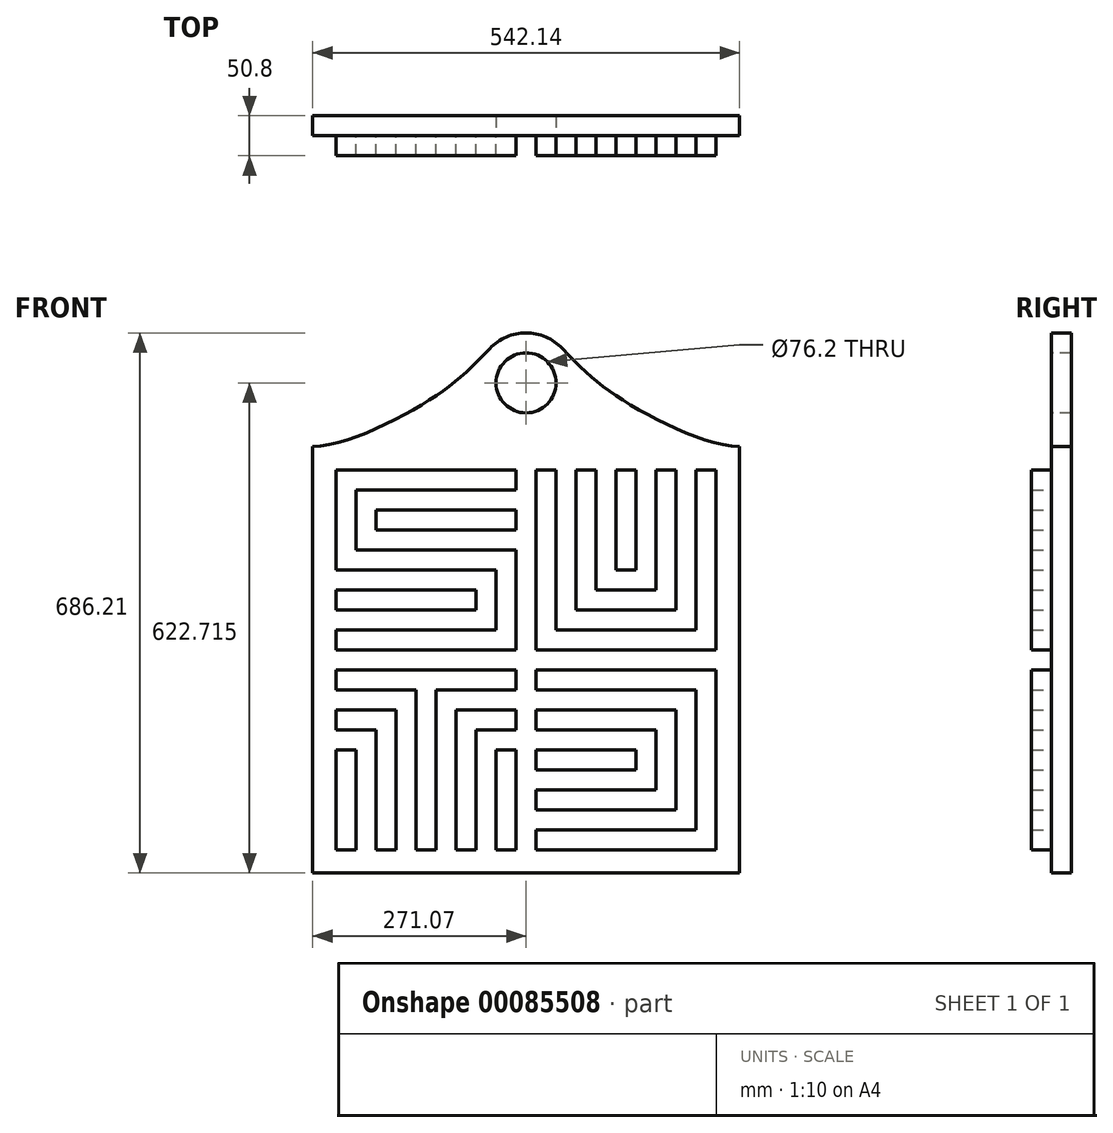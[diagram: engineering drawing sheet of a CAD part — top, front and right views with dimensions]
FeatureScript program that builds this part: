
annotation { "Feature Type Name" : "Feature", "Feature Type Description" : "" }
export const myFeature = defineFeature(function(context is Context, id is Id, definition is map)
    precondition{}
    {
        {
            var Q0;
            Q0=qCreatedBy(makeId("Front.planeOp"),FACE);
            var sketch = newSketch(context, id + "F0", { "sketchPlane" : qUnion([Q0])});
            skLineSegment(sketch, "E0.bottom", {"start": v(-114.3, 114.3) * mm, "end": v(114.3, 114.3) * mm});
            skLineSegment(sketch, "E0.top", {"start": v(-114.3, -114.3) * mm, "end": v(114.3, -114.3) * mm});
            skLineSegment(sketch, "E0.left", {"start": v(-114.3, 114.3) * mm, "end": v(-114.3, -114.3) * mm});
            skLineSegment(sketch, "E0.right", {"start": v(114.3, 114.3) * mm, "end": v(114.3, -114.3) * mm});
            skPoint(sketch, "E0.middle", {"position": v(0, 0) * mm});
            skLineSegment(sketch, "E1.1.0.0", {"start": v(-88.9, 114.3) * mm, "end": v(-88.9, -114.3) * mm});
            skLineSegment(sketch, "E1.2.0.0", {"start": v(-63.5, 114.3) * mm, "end": v(-63.5, -114.3) * mm});
            skLineSegment(sketch, "E1.3.0.0", {"start": v(-38.1, 114.3) * mm, "end": v(-38.1, -114.3) * mm});
            skLineSegment(sketch, "E1.4.0.0", {"start": v(-12.7, 114.3) * mm, "end": v(-12.7, -114.3) * mm});
            skLineSegment(sketch, "E1.5.0.0", {"start": v(12.7, 114.3) * mm, "end": v(12.7, -114.3) * mm});
            skLineSegment(sketch, "E1.6.0.0", {"start": v(38.1, 114.3) * mm, "end": v(38.1, -114.3) * mm});
            skLineSegment(sketch, "E1.7.0.0", {"start": v(63.5, 114.3) * mm, "end": v(63.5, -114.3) * mm});
            skLineSegment(sketch, "E1.8.0.0", {"start": v(88.9, 114.3) * mm, "end": v(88.9, -114.3) * mm});
            skLineSegment(sketch, "E1.direction1", {"start": v(-114.3, -114.3) * mm, "end": v(-88.9, -114.3) * mm, "construction": true});
            skLineSegment(sketch, "E2.0.1.0", {"start": v(-114.3, 88.9) * mm, "end": v(114.3, 88.9) * mm});
            skLineSegment(sketch, "E2.0.2.0", {"start": v(-114.3, 63.5) * mm, "end": v(114.3, 63.5) * mm});
            skLineSegment(sketch, "E2.0.3.0", {"start": v(-114.3, 38.1) * mm, "end": v(114.3, 38.1) * mm});
            skLineSegment(sketch, "E2.0.4.0", {"start": v(-114.3, 12.7) * mm, "end": v(114.3, 12.7) * mm});
            skLineSegment(sketch, "E2.0.5.0", {"start": v(-114.3, -12.7) * mm, "end": v(114.3, -12.7) * mm});
            skLineSegment(sketch, "E2.0.6.0", {"start": v(-114.3, -38.1) * mm, "end": v(114.3, -38.1) * mm});
            skLineSegment(sketch, "E2.0.7.0", {"start": v(-114.3, -63.5) * mm, "end": v(114.3, -63.5) * mm});
            skLineSegment(sketch, "E2.0.8.0", {"start": v(-114.3, -88.9) * mm, "end": v(114.3, -88.9) * mm});
            skLineSegment(sketch, "E2.direction1", {"start": v(-114.3, 114.3) * mm, "end": v(-88.9, 114.3) * mm, "construction": true});
            skLineSegment(sketch, "E2.direction2", {"start": v(-114.3, 114.3) * mm, "end": v(-114.3, 88.9) * mm, "construction": true});
            skLineSegment(sketch, "E3.0.1.0", {"start": v(-12.7, -139.7) * mm, "end": v(-12.7, -368.3) * mm});
            skLineSegment(sketch, "E3.0.1.1", {"start": v(-88.9, -139.7) * mm, "end": v(-88.9, -368.3) * mm});
            skLineSegment(sketch, "E3.0.1.2", {"start": v(-38.1, -139.7) * mm, "end": v(-38.1, -368.3) * mm});
            skLineSegment(sketch, "E3.0.1.3", {"start": v(-114.3, -165.1) * mm, "end": v(114.3, -165.1) * mm});
            skLineSegment(sketch, "E3.0.1.4", {"start": v(-114.3, -190.5) * mm, "end": v(114.3, -190.5) * mm});
            skLineSegment(sketch, "E3.0.1.5", {"start": v(-63.5, -139.7) * mm, "end": v(-63.5, -368.3) * mm});
            skLineSegment(sketch, "E3.0.1.6", {"start": v(-114.3, -215.9) * mm, "end": v(114.3, -215.9) * mm});
            skLineSegment(sketch, "E3.0.1.7", {"start": v(-114.3, -139.7) * mm, "end": v(114.3, -139.7) * mm});
            skLineSegment(sketch, "E3.0.1.8", {"start": v(-114.3, -368.3) * mm, "end": v(114.3, -368.3) * mm});
            skLineSegment(sketch, "E3.0.1.9", {"start": v(-114.3, -139.7) * mm, "end": v(-114.3, -368.3) * mm});
            skLineSegment(sketch, "E3.0.1.10", {"start": v(114.3, -139.7) * mm, "end": v(114.3, -368.3) * mm});
            skLineSegment(sketch, "E3.0.1.11", {"start": v(12.7, -139.7) * mm, "end": v(12.7, -368.3) * mm});
            skLineSegment(sketch, "E3.0.1.12", {"start": v(38.1, -139.7) * mm, "end": v(38.1, -368.3) * mm});
            skLineSegment(sketch, "E3.0.1.13", {"start": v(63.5, -139.7) * mm, "end": v(63.5, -368.3) * mm});
            skLineSegment(sketch, "E3.0.1.14", {"start": v(88.9, -139.7) * mm, "end": v(88.9, -368.3) * mm});
            skLineSegment(sketch, "E3.0.1.15", {"start": v(-114.3, -241.3) * mm, "end": v(114.3, -241.3) * mm});
            skLineSegment(sketch, "E3.0.1.16", {"start": v(-114.3, -266.7) * mm, "end": v(114.3, -266.7) * mm});
            skPoint(sketch, "E3.0.1.17", {"position": v(0, -254) * mm});
            skLineSegment(sketch, "E3.0.1.18", {"start": v(-114.3, -342.9) * mm, "end": v(114.3, -342.9) * mm});
            skLineSegment(sketch, "E3.0.1.19", {"start": v(-114.3, -292.1) * mm, "end": v(114.3, -292.1) * mm});
            skLineSegment(sketch, "E3.0.1.20", {"start": v(-114.3, -317.5) * mm, "end": v(114.3, -317.5) * mm});
            skLineSegment(sketch, "E3.0.1.21", {"start": v(-114.3, -139.7) * mm, "end": v(-114.3, -165.1) * mm, "construction": true});
            skLineSegment(sketch, "E3.0.1.22", {"start": v(-114.3, -368.3) * mm, "end": v(-88.9, -368.3) * mm, "construction": true});
            skLineSegment(sketch, "E3.0.1.23", {"start": v(-114.3, -139.7) * mm, "end": v(-88.9, -139.7) * mm, "construction": true});
            skLineSegment(sketch, "E3.1.0.0", {"start": v(241.3, 114.3) * mm, "end": v(241.3, -88.9) * mm});
            skLineSegment(sketch, "E3.1.0.1", {"start": v(165.1, 114.3) * mm, "end": v(165.1, -88.9) * mm});
            skLineSegment(sketch, "E3.1.0.2", {"start": v(215.9, 114.3) * mm, "end": v(215.9, -88.9) * mm});
            skLineSegment(sketch, "E3.1.0.3", {"start": v(165.1, 88.9) * mm, "end": v(190.5, 88.9) * mm});
            skLineSegment(sketch, "E3.1.0.4", {"start": v(165.1, 63.5) * mm, "end": v(342.9, 63.5) * mm});
            skLineSegment(sketch, "E3.1.0.5", {"start": v(190.5, 114.3) * mm, "end": v(190.5, -88.9) * mm});
            skLineSegment(sketch, "E3.1.0.6", {"start": v(165.1, 38.1) * mm, "end": v(342.9, 38.1) * mm});
            skLineSegment(sketch, "E3.1.0.7", {"start": v(139.7, 114.3) * mm, "end": v(368.3, 114.3) * mm});
            skLineSegment(sketch, "E3.1.0.8", {"start": v(139.7, -114.3) * mm, "end": v(368.3, -114.3) * mm});
            skLineSegment(sketch, "E3.1.0.9", {"start": v(139.7, 114.3) * mm, "end": v(139.7, -114.3) * mm});
            skLineSegment(sketch, "E3.1.0.10", {"start": v(368.3, 114.3) * mm, "end": v(368.3, -114.3) * mm});
            skLineSegment(sketch, "E3.1.0.11", {"start": v(266.7, 114.3) * mm, "end": v(266.7, -88.9) * mm});
            skLineSegment(sketch, "E3.1.0.12", {"start": v(292.1, 114.3) * mm, "end": v(292.1, -88.9) * mm});
            skLineSegment(sketch, "E3.1.0.13", {"start": v(317.5, 114.3) * mm, "end": v(317.5, -88.9) * mm});
            skLineSegment(sketch, "E3.1.0.14", {"start": v(342.9, 114.3) * mm, "end": v(342.9, -88.9) * mm});
            skLineSegment(sketch, "E3.1.0.15", {"start": v(165.1, 12.7) * mm, "end": v(342.9, 12.7) * mm});
            skLineSegment(sketch, "E3.1.0.16", {"start": v(165.1, -12.7) * mm, "end": v(342.9, -12.7) * mm});
            skPoint(sketch, "E3.1.0.17", {"position": v(254, 0) * mm});
            skLineSegment(sketch, "E3.1.0.18", {"start": v(165.1, -88.9) * mm, "end": v(342.9, -88.9) * mm});
            skLineSegment(sketch, "E3.1.0.19", {"start": v(165.1, -38.1) * mm, "end": v(342.9, -38.1) * mm});
            skLineSegment(sketch, "E3.1.0.20", {"start": v(165.1, -63.5) * mm, "end": v(342.9, -63.5) * mm});
            skLineSegment(sketch, "E3.1.0.21", {"start": v(139.7, 114.3) * mm, "end": v(139.7, 88.9) * mm, "construction": true});
            skLineSegment(sketch, "E3.1.0.22", {"start": v(139.7, -114.3) * mm, "end": v(165.1, -114.3) * mm, "construction": true});
            skLineSegment(sketch, "E3.1.0.23", {"start": v(139.7, 114.3) * mm, "end": v(165.1, 114.3) * mm, "construction": true});
            skLineSegment(sketch, "E3.1.1.0", {"start": v(241.3, -139.7) * mm, "end": v(241.3, -368.3) * mm});
            skLineSegment(sketch, "E3.1.1.1", {"start": v(165.1, -139.7) * mm, "end": v(165.1, -368.3) * mm});
            skLineSegment(sketch, "E3.1.1.2", {"start": v(215.9, -139.7) * mm, "end": v(215.9, -368.3) * mm});
            skLineSegment(sketch, "E3.1.1.3", {"start": v(139.7, -165.1) * mm, "end": v(368.3, -165.1) * mm});
            skLineSegment(sketch, "E3.1.1.4", {"start": v(139.7, -190.5) * mm, "end": v(368.3, -190.5) * mm});
            skLineSegment(sketch, "E3.1.1.5", {"start": v(190.5, -139.7) * mm, "end": v(190.5, -368.3) * mm});
            skLineSegment(sketch, "E3.1.1.6", {"start": v(139.7, -215.9) * mm, "end": v(368.3, -215.9) * mm});
            skLineSegment(sketch, "E3.1.1.7", {"start": v(139.7, -139.7) * mm, "end": v(368.3, -139.7) * mm});
            skLineSegment(sketch, "E3.1.1.8", {"start": v(139.7, -368.3) * mm, "end": v(368.3, -368.3) * mm});
            skLineSegment(sketch, "E3.1.1.9", {"start": v(139.7, -139.7) * mm, "end": v(139.7, -368.3) * mm});
            skLineSegment(sketch, "E3.1.1.10", {"start": v(368.3, -139.7) * mm, "end": v(368.3, -368.3) * mm});
            skLineSegment(sketch, "E3.1.1.11", {"start": v(266.7, -139.7) * mm, "end": v(266.7, -368.3) * mm});
            skLineSegment(sketch, "E3.1.1.12", {"start": v(292.1, -139.7) * mm, "end": v(292.1, -368.3) * mm});
            skLineSegment(sketch, "E3.1.1.13", {"start": v(317.5, -139.7) * mm, "end": v(317.5, -368.3) * mm});
            skLineSegment(sketch, "E3.1.1.14", {"start": v(342.9, -139.7) * mm, "end": v(342.9, -368.3) * mm});
            skLineSegment(sketch, "E3.1.1.15", {"start": v(139.7, -241.3) * mm, "end": v(368.3, -241.3) * mm});
            skLineSegment(sketch, "E3.1.1.16", {"start": v(139.7, -266.7) * mm, "end": v(368.3, -266.7) * mm});
            skPoint(sketch, "E3.1.1.17", {"position": v(254, -254) * mm});
            skLineSegment(sketch, "E3.1.1.18", {"start": v(139.7, -342.9) * mm, "end": v(368.3, -342.9) * mm});
            skLineSegment(sketch, "E3.1.1.19", {"start": v(139.7, -292.1) * mm, "end": v(368.3, -292.1) * mm});
            skLineSegment(sketch, "E3.1.1.20", {"start": v(139.7, -317.5) * mm, "end": v(368.3, -317.5) * mm});
            skLineSegment(sketch, "E3.1.1.21", {"start": v(139.7, -139.7) * mm, "end": v(139.7, -165.1) * mm, "construction": true});
            skLineSegment(sketch, "E3.1.1.22", {"start": v(139.7, -368.3) * mm, "end": v(165.1, -368.3) * mm, "construction": true});
            skLineSegment(sketch, "E3.1.1.23", {"start": v(139.7, -139.7) * mm, "end": v(165.1, -139.7) * mm, "construction": true});
            skLineSegment(sketch, "E3.direction1", {"start": v(-12.7, -114.3) * mm, "end": v(241.3, -114.3) * mm, "construction": true});
            skLineSegment(sketch, "E3.direction2", {"start": v(-12.7, -114.3) * mm, "end": v(-12.7, -368.3) * mm, "construction": true});
            skPoint(sketch, "E4.orphan", {"position": v(139.7, 63.5) * mm});
            skPoint(sketch, "E5.orphan", {"position": v(139.7, 38.1) * mm});
            skPoint(sketch, "E6.orphan", {"position": v(139.7, 12.7) * mm});
            skPoint(sketch, "E7.orphan", {"position": v(139.7, -12.7) * mm});
            skPoint(sketch, "E8.orphan", {"position": v(139.7, -38.1) * mm});
            skPoint(sketch, "E9.orphan", {"position": v(139.7, -63.5) * mm});
            skPoint(sketch, "E10.orphan", {"position": v(139.7, -88.9) * mm});
            skPoint(sketch, "E11.orphan", {"position": v(190.5, -114.3) * mm});
            skPoint(sketch, "E12.orphan", {"position": v(215.9, -114.3) * mm});
            skPoint(sketch, "E13.orphan", {"position": v(266.7, -114.3) * mm});
            skPoint(sketch, "E14.orphan", {"position": v(292.1, -114.3) * mm});
            skPoint(sketch, "E15.orphan", {"position": v(317.5, -114.3) * mm});
            skPoint(sketch, "E16.orphan", {"position": v(342.9, -114.3) * mm});
            skPoint(sketch, "E17.orphan", {"position": v(368.3, -88.9) * mm});
            skPoint(sketch, "E18.orphan", {"position": v(368.3, -63.5) * mm});
            skPoint(sketch, "E19.orphan", {"position": v(368.3, -38.1) * mm});
            skPoint(sketch, "E20.orphan", {"position": v(368.3, -12.7) * mm});
            skPoint(sketch, "E21.orphan", {"position": v(368.3, 12.7) * mm});
            skPoint(sketch, "E22.orphan", {"position": v(368.3, 38.1) * mm});
            skPoint(sketch, "E23.orphan", {"position": v(368.3, 63.5) * mm});
            skPoint(sketch, "E24.orphan", {"position": v(368.3, 88.9) * mm});
            skLineSegment(sketch, "E25.trimOffspring", {"start": v(215.9, 88.9) * mm, "end": v(342.9, 88.9) * mm});
            skSolve(sketch);
        }
        {
            var Q0;
            {var subQ0=sQuery(id+"F0.wireOp",EDGE,"E0.right");var subQ1=sQuery(id+"F0.wireOp",EDGE,"E0.bottom");var subQ2=makeQuery(id+"F0.imprint","INTERSECT",VERTEX,{"derivedFrom":[subQ1,subQ0]});Q0=makeQuery(id+"F0.imprint","IMPRINT",FACE,{"disambiguationData":[TD([[makeQuery(id+"F0.imprint","IMPRINT",EDGE,{"disambiguationData":[TD([[subQ2,1.0]])],"derivedFrom":subQ1}),-1.0]])]});}
            var Q1;
            {var subQ0=sQuery(id+"F0.wireOp",EDGE,"E1.7.0.0");var subQ1=sQuery(id+"F0.wireOp",EDGE,"E0.bottom");var subQ2=makeQuery(id+"F0.imprint","INTERSECT",VERTEX,{"derivedFrom":[subQ1,subQ0]});Q1=makeQuery(id+"F0.imprint","IMPRINT",FACE,{"disambiguationData":[TD([[makeQuery(id+"F0.imprint","IMPRINT",EDGE,{"disambiguationData":[TD([[subQ2,-1.0]])],"derivedFrom":subQ1}),-1.0]])]});}
            var Q2;
            {var subQ0=sQuery(id+"F0.wireOp",EDGE,"E1.6.0.0");var subQ1=sQuery(id+"F0.wireOp",EDGE,"E0.bottom");var subQ2=makeQuery(id+"F0.imprint","INTERSECT",VERTEX,{"derivedFrom":[subQ1,subQ0]});Q2=makeQuery(id+"F0.imprint","IMPRINT",FACE,{"disambiguationData":[TD([[makeQuery(id+"F0.imprint","IMPRINT",EDGE,{"disambiguationData":[TD([[subQ2,-1.0]])],"derivedFrom":subQ1}),-1.0]])]});}
            var Q3;
            {var subQ0=sQuery(id+"F0.wireOp",EDGE,"E1.5.0.0");var subQ1=sQuery(id+"F0.wireOp",EDGE,"E0.bottom");var subQ2=makeQuery(id+"F0.imprint","INTERSECT",VERTEX,{"derivedFrom":[subQ1,subQ0]});Q3=makeQuery(id+"F0.imprint","IMPRINT",FACE,{"disambiguationData":[TD([[makeQuery(id+"F0.imprint","IMPRINT",EDGE,{"disambiguationData":[TD([[subQ2,-1.0]])],"derivedFrom":subQ1}),-1.0]])]});}
            var Q4;
            {var subQ0=sQuery(id+"F0.wireOp",EDGE,"E1.4.0.0");var subQ1=sQuery(id+"F0.wireOp",EDGE,"E0.bottom");var subQ2=makeQuery(id+"F0.imprint","INTERSECT",VERTEX,{"derivedFrom":[subQ1,subQ0]});Q4=makeQuery(id+"F0.imprint","IMPRINT",FACE,{"disambiguationData":[TD([[makeQuery(id+"F0.imprint","IMPRINT",EDGE,{"disambiguationData":[TD([[subQ2,-1.0]])],"derivedFrom":subQ1}),-1.0]])]});}
            var Q5;
            {var subQ0=sQuery(id+"F0.wireOp",EDGE,"E1.3.0.0");var subQ1=sQuery(id+"F0.wireOp",EDGE,"E0.bottom");var subQ2=makeQuery(id+"F0.imprint","INTERSECT",VERTEX,{"derivedFrom":[subQ1,subQ0]});Q5=makeQuery(id+"F0.imprint","IMPRINT",FACE,{"disambiguationData":[TD([[makeQuery(id+"F0.imprint","IMPRINT",EDGE,{"disambiguationData":[TD([[subQ2,-1.0]])],"derivedFrom":subQ1}),-1.0]])]});}
            var Q6;
            {var subQ0=sQuery(id+"F0.wireOp",EDGE,"E1.2.0.0");var subQ1=sQuery(id+"F0.wireOp",EDGE,"E0.bottom");var subQ2=makeQuery(id+"F0.imprint","INTERSECT",VERTEX,{"derivedFrom":[subQ1,subQ0]});Q6=makeQuery(id+"F0.imprint","IMPRINT",FACE,{"disambiguationData":[TD([[makeQuery(id+"F0.imprint","IMPRINT",EDGE,{"disambiguationData":[TD([[subQ2,-1.0]])],"derivedFrom":subQ1}),-1.0]])]});}
            var Q7;
            {var subQ0=sQuery(id+"F0.wireOp",EDGE,"E1.1.0.0");var subQ1=sQuery(id+"F0.wireOp",EDGE,"E0.bottom");var subQ2=makeQuery(id+"F0.imprint","INTERSECT",VERTEX,{"derivedFrom":[subQ1,subQ0]});Q7=makeQuery(id+"F0.imprint","IMPRINT",FACE,{"disambiguationData":[TD([[makeQuery(id+"F0.imprint","IMPRINT",EDGE,{"disambiguationData":[TD([[subQ2,-1.0]])],"derivedFrom":subQ1}),-1.0]])]});}
            var Q8;
            {var subQ0=sQuery(id+"F0.wireOp",EDGE,"E0.left");var subQ1=sQuery(id+"F0.wireOp",EDGE,"E0.bottom");var subQ2=makeQuery(id+"F0.imprint","INTERSECT",VERTEX,{"derivedFrom":[subQ1,subQ0]});Q8=makeQuery(id+"F0.imprint","IMPRINT",FACE,{"disambiguationData":[TD([[makeQuery(id+"F0.imprint","IMPRINT",EDGE,{"disambiguationData":[TD([[subQ2,-1.0]])],"derivedFrom":subQ1}),-1.0]])]});}
            var Q9;
            {var subQ0=sQuery(id+"F0.wireOp",EDGE,"E2.0.1.0");var subQ1=sQuery(id+"F0.wireOp",EDGE,"E0.left");var subQ2=makeQuery(id+"F0.imprint","INTERSECT",VERTEX,{"derivedFrom":[subQ1,subQ0]});Q9=makeQuery(id+"F0.imprint","IMPRINT",FACE,{"disambiguationData":[TD([[makeQuery(id+"F0.imprint","IMPRINT",EDGE,{"disambiguationData":[TD([[subQ2,-1.0]])],"derivedFrom":subQ1}),1.0]])]});}
            var Q10;
            {var subQ0=sQuery(id+"F0.wireOp",EDGE,"E2.0.2.0");var subQ1=sQuery(id+"F0.wireOp",EDGE,"E0.left");var subQ2=makeQuery(id+"F0.imprint","INTERSECT",VERTEX,{"derivedFrom":[subQ1,subQ0]});Q10=makeQuery(id+"F0.imprint","IMPRINT",FACE,{"disambiguationData":[TD([[makeQuery(id+"F0.imprint","IMPRINT",EDGE,{"disambiguationData":[TD([[subQ2,-1.0]])],"derivedFrom":subQ1}),1.0]])]});}
            var Q11;
            {var subQ0=sQuery(id+"F0.wireOp",EDGE,"E2.0.3.0");var subQ1=sQuery(id+"F0.wireOp",EDGE,"E0.left");var subQ2=makeQuery(id+"F0.imprint","INTERSECT",VERTEX,{"derivedFrom":[subQ1,subQ0]});Q11=makeQuery(id+"F0.imprint","IMPRINT",FACE,{"disambiguationData":[TD([[makeQuery(id+"F0.imprint","IMPRINT",EDGE,{"disambiguationData":[TD([[subQ2,-1.0]])],"derivedFrom":subQ1}),1.0]])]});}
            var Q12;
            {var subQ0=sQuery(id+"F0.wireOp",EDGE,"E2.0.4.0");var subQ1=sQuery(id+"F0.wireOp",EDGE,"E0.left");var subQ2=makeQuery(id+"F0.imprint","INTERSECT",VERTEX,{"derivedFrom":[subQ1,subQ0]});Q12=makeQuery(id+"F0.imprint","IMPRINT",FACE,{"disambiguationData":[TD([[makeQuery(id+"F0.imprint","IMPRINT",EDGE,{"disambiguationData":[TD([[subQ2,-1.0]])],"derivedFrom":subQ1}),1.0]])]});}
            var Q13;
            {var subQ0=sQuery(id+"F0.wireOp",EDGE,"E2.0.4.0");var subQ1=sQuery(id+"F0.wireOp",EDGE,"E1.1.0.0");var subQ2=makeQuery(id+"F0.imprint","INTERSECT",VERTEX,{"derivedFrom":[subQ1,subQ0]});Q13=makeQuery(id+"F0.imprint","IMPRINT",FACE,{"disambiguationData":[TD([[makeQuery(id+"F0.imprint","IMPRINT",EDGE,{"disambiguationData":[TD([[subQ2,-1.0]])],"derivedFrom":subQ1}),1.0]])]});}
            var Q14;
            {var subQ0=sQuery(id+"F0.wireOp",EDGE,"E2.0.4.0");var subQ1=sQuery(id+"F0.wireOp",EDGE,"E1.2.0.0");var subQ2=makeQuery(id+"F0.imprint","INTERSECT",VERTEX,{"derivedFrom":[subQ1,subQ0]});Q14=makeQuery(id+"F0.imprint","IMPRINT",FACE,{"disambiguationData":[TD([[makeQuery(id+"F0.imprint","IMPRINT",EDGE,{"disambiguationData":[TD([[subQ2,-1.0]])],"derivedFrom":subQ1}),1.0]])]});}
            var Q15;
            {var subQ0=sQuery(id+"F0.wireOp",EDGE,"E2.0.4.0");var subQ1=sQuery(id+"F0.wireOp",EDGE,"E1.3.0.0");var subQ2=makeQuery(id+"F0.imprint","INTERSECT",VERTEX,{"derivedFrom":[subQ1,subQ0]});Q15=makeQuery(id+"F0.imprint","IMPRINT",FACE,{"disambiguationData":[TD([[makeQuery(id+"F0.imprint","IMPRINT",EDGE,{"disambiguationData":[TD([[subQ2,-1.0]])],"derivedFrom":subQ1}),1.0]])]});}
            var Q16;
            {var subQ0=sQuery(id+"F0.wireOp",EDGE,"E2.0.4.0");var subQ1=sQuery(id+"F0.wireOp",EDGE,"E1.4.0.0");var subQ2=makeQuery(id+"F0.imprint","INTERSECT",VERTEX,{"derivedFrom":[subQ1,subQ0]});Q16=makeQuery(id+"F0.imprint","IMPRINT",FACE,{"disambiguationData":[TD([[makeQuery(id+"F0.imprint","IMPRINT",EDGE,{"disambiguationData":[TD([[subQ2,-1.0]])],"derivedFrom":subQ1}),1.0]])]});}
            var Q17;
            {var subQ0=sQuery(id+"F0.wireOp",EDGE,"E2.0.4.0");var subQ1=sQuery(id+"F0.wireOp",EDGE,"E1.5.0.0");var subQ2=makeQuery(id+"F0.imprint","INTERSECT",VERTEX,{"derivedFrom":[subQ1,subQ0]});Q17=makeQuery(id+"F0.imprint","IMPRINT",FACE,{"disambiguationData":[TD([[makeQuery(id+"F0.imprint","IMPRINT",EDGE,{"disambiguationData":[TD([[subQ2,-1.0]])],"derivedFrom":subQ1}),1.0]])]});}
            var Q18;
            {var subQ0=sQuery(id+"F0.wireOp",EDGE,"E2.0.4.0");var subQ1=sQuery(id+"F0.wireOp",EDGE,"E1.6.0.0");var subQ2=makeQuery(id+"F0.imprint","INTERSECT",VERTEX,{"derivedFrom":[subQ1,subQ0]});Q18=makeQuery(id+"F0.imprint","IMPRINT",FACE,{"disambiguationData":[TD([[makeQuery(id+"F0.imprint","IMPRINT",EDGE,{"disambiguationData":[TD([[subQ2,-1.0]])],"derivedFrom":subQ1}),1.0]])]});}
            var Q19;
            {var subQ0=sQuery(id+"F0.wireOp",EDGE,"E2.0.4.0");var subQ1=sQuery(id+"F0.wireOp",EDGE,"E1.7.0.0");var subQ2=makeQuery(id+"F0.imprint","INTERSECT",VERTEX,{"derivedFrom":[subQ1,subQ0]});Q19=makeQuery(id+"F0.imprint","IMPRINT",FACE,{"disambiguationData":[TD([[makeQuery(id+"F0.imprint","IMPRINT",EDGE,{"disambiguationData":[TD([[subQ2,-1.0]])],"derivedFrom":subQ1}),1.0]])]});}
            var Q20;
            {var subQ0=sQuery(id+"F0.wireOp",EDGE,"E2.0.4.0");var subQ1=sQuery(id+"F0.wireOp",EDGE,"E0.right");var subQ2=makeQuery(id+"F0.imprint","INTERSECT",VERTEX,{"derivedFrom":[subQ1,subQ0]});Q20=makeQuery(id+"F0.imprint","IMPRINT",FACE,{"disambiguationData":[TD([[makeQuery(id+"F0.imprint","IMPRINT",EDGE,{"disambiguationData":[TD([[subQ2,-1.0]])],"derivedFrom":subQ1}),-1.0]])]});}
            extrude(context, id + "F1", {"entities" : qUnion([Q0, Q1, Q2, Q3, Q4, Q5, Q6, Q7, Q8, Q9, Q10, Q11, Q12, Q13, Q14, Q15, Q16, Q17, Q18, Q19, Q20]), "depth" : 25.4 * mm});
        }
        {
            var Q0;
            Q0=makeQuery(id+"F0.imprint","IMPRINT",FACE,{"disambiguationData":[TD([[makeQuery(id+"F0.imprint","IMPRINT",EDGE,{"derivedFrom":sQuery(id+"F0.wireOp",EDGE,"E3.1.0.8")}),1.0]])]});
            var Q1;
            {var subQ1=sQuery(id+"F0.wireOp",EDGE,"E3.1.0.2");var subQ6=sQuery(id+"F0.wireOp",EDGE,"E3.1.0.7");var subQ9=makeQuery(id+"F0.imprint","INTERSECT",VERTEX,{"derivedFrom":[subQ1,subQ6]});Q1=makeQuery(id+"F0.imprint","IMPRINT",FACE,{"disambiguationData":[TD([[makeQuery(id+"F0.imprint","IMPRINT",EDGE,{"disambiguationData":[TD([[subQ9,-1.0]])],"derivedFrom":subQ1}),-1.0]])]});}
            var Q2;
            {var subQ0=sQuery(id+"F0.wireOp",EDGE,"E3.1.0.4");var subQ1=sQuery(id+"F0.wireOp",EDGE,"E3.1.0.2");var subQ2=makeQuery(id+"F0.imprint","INTERSECT",VERTEX,{"derivedFrom":[subQ1,subQ0]});Q2=makeQuery(id+"F0.imprint","IMPRINT",FACE,{"disambiguationData":[TD([[makeQuery(id+"F0.imprint","IMPRINT",EDGE,{"disambiguationData":[TD([[subQ2,-1.0]])],"derivedFrom":subQ1}),-1.0]])]});}
            var Q3;
            {var subQ0=sQuery(id+"F0.wireOp",EDGE,"E3.1.0.6");var subQ1=sQuery(id+"F0.wireOp",EDGE,"E3.1.0.2");var subQ2=makeQuery(id+"F0.imprint","INTERSECT",VERTEX,{"derivedFrom":[subQ1,subQ0]});Q3=makeQuery(id+"F0.imprint","IMPRINT",FACE,{"disambiguationData":[TD([[makeQuery(id+"F0.imprint","IMPRINT",EDGE,{"disambiguationData":[TD([[subQ2,-1.0]])],"derivedFrom":subQ1}),-1.0]])]});}
            var Q4;
            {var subQ0=sQuery(id+"F0.wireOp",EDGE,"E3.1.0.15");var subQ1=sQuery(id+"F0.wireOp",EDGE,"E3.1.0.2");var subQ2=makeQuery(id+"F0.imprint","INTERSECT",VERTEX,{"derivedFrom":[subQ1,subQ0]});Q4=makeQuery(id+"F0.imprint","IMPRINT",FACE,{"disambiguationData":[TD([[makeQuery(id+"F0.imprint","IMPRINT",EDGE,{"disambiguationData":[TD([[subQ2,-1.0]])],"derivedFrom":subQ1}),-1.0]])]});}
            var Q5;
            {var subQ0=sQuery(id+"F0.wireOp",EDGE,"E3.1.0.16");var subQ1=sQuery(id+"F0.wireOp",EDGE,"E3.1.0.2");var subQ2=makeQuery(id+"F0.imprint","INTERSECT",VERTEX,{"derivedFrom":[subQ1,subQ0]});Q5=makeQuery(id+"F0.imprint","IMPRINT",FACE,{"disambiguationData":[TD([[makeQuery(id+"F0.imprint","IMPRINT",EDGE,{"disambiguationData":[TD([[subQ2,-1.0]])],"derivedFrom":subQ1}),-1.0]])]});}
            var Q6;
            {var subQ0=sQuery(id+"F0.wireOp",EDGE,"E3.1.0.19");var subQ1=sQuery(id+"F0.wireOp",EDGE,"E3.1.0.2");var subQ2=makeQuery(id+"F0.imprint","INTERSECT",VERTEX,{"derivedFrom":[subQ1,subQ0]});Q6=makeQuery(id+"F0.imprint","IMPRINT",FACE,{"disambiguationData":[TD([[makeQuery(id+"F0.imprint","IMPRINT",EDGE,{"disambiguationData":[TD([[subQ2,-1.0]])],"derivedFrom":subQ1}),-1.0]])]});}
            var Q7;
            {var subQ0=sQuery(id+"F0.wireOp",EDGE,"E3.1.0.19");var subQ1=sQuery(id+"F0.wireOp",EDGE,"E3.1.0.11");var subQ2=makeQuery(id+"F0.imprint","INTERSECT",VERTEX,{"derivedFrom":[subQ1,subQ0]});Q7=makeQuery(id+"F0.imprint","IMPRINT",FACE,{"disambiguationData":[TD([[makeQuery(id+"F0.imprint","IMPRINT",EDGE,{"disambiguationData":[TD([[subQ2,-1.0]])],"derivedFrom":subQ1}),1.0]])]});}
            var Q8;
            {var subQ0=sQuery(id+"F0.wireOp",EDGE,"E3.1.0.19");var subQ1=sQuery(id+"F0.wireOp",EDGE,"E3.1.0.12");var subQ2=makeQuery(id+"F0.imprint","INTERSECT",VERTEX,{"derivedFrom":[subQ1,subQ0]});Q8=makeQuery(id+"F0.imprint","IMPRINT",FACE,{"disambiguationData":[TD([[makeQuery(id+"F0.imprint","IMPRINT",EDGE,{"disambiguationData":[TD([[subQ2,-1.0]])],"derivedFrom":subQ1}),1.0]])]});}
            var Q9;
            {var subQ0=sQuery(id+"F0.wireOp",EDGE,"E3.1.0.19");var subQ1=sQuery(id+"F0.wireOp",EDGE,"E3.1.0.0");var subQ2=makeQuery(id+"F0.imprint","INTERSECT",VERTEX,{"derivedFrom":[subQ1,subQ0]});Q9=makeQuery(id+"F0.imprint","IMPRINT",FACE,{"disambiguationData":[TD([[makeQuery(id+"F0.imprint","IMPRINT",EDGE,{"disambiguationData":[TD([[subQ2,-1.0]])],"derivedFrom":subQ1}),-1.0]])]});}
            var Q10;
            {var subQ0=sQuery(id+"F0.wireOp",EDGE,"E3.1.0.19");var subQ1=sQuery(id+"F0.wireOp",EDGE,"E3.1.0.0");var subQ2=makeQuery(id+"F0.imprint","INTERSECT",VERTEX,{"derivedFrom":[subQ1,subQ0]});Q10=makeQuery(id+"F0.imprint","IMPRINT",FACE,{"disambiguationData":[TD([[makeQuery(id+"F0.imprint","IMPRINT",EDGE,{"disambiguationData":[TD([[subQ2,-1.0]])],"derivedFrom":subQ1}),1.0]])]});}
            var Q11;
            {var subQ0=sQuery(id+"F0.wireOp",EDGE,"E3.1.0.12");var subQ1=sQuery(id+"F0.wireOp",EDGE,"E3.1.0.4");var subQ2=makeQuery(id+"F0.imprint","INTERSECT",VERTEX,{"derivedFrom":[subQ1,subQ0]});Q11=makeQuery(id+"F0.imprint","IMPRINT",FACE,{"disambiguationData":[TD([[makeQuery(id+"F0.imprint","IMPRINT",EDGE,{"disambiguationData":[TD([[subQ2,-1.0]])],"derivedFrom":subQ1}),1.0]])]});}
            var Q12;
            {var subQ0=sQuery(id+"F0.wireOp",EDGE,"E3.1.0.12");var subQ1=sQuery(id+"F0.wireOp",EDGE,"E3.1.0.7");var subQ2=makeQuery(id+"F0.imprint","INTERSECT",VERTEX,{"derivedFrom":[subQ1,subQ0]});Q12=makeQuery(id+"F0.imprint","IMPRINT",FACE,{"disambiguationData":[TD([[makeQuery(id+"F0.imprint","IMPRINT",EDGE,{"disambiguationData":[TD([[subQ2,-1.0]])],"derivedFrom":subQ1}),-1.0]])]});}
            var Q13;
            {var subQ0=sQuery(id+"F0.wireOp",EDGE,"E3.1.0.12");var subQ1=sQuery(id+"F0.wireOp",EDGE,"E3.1.0.6");var subQ2=makeQuery(id+"F0.imprint","INTERSECT",VERTEX,{"derivedFrom":[subQ1,subQ0]});Q13=makeQuery(id+"F0.imprint","IMPRINT",FACE,{"disambiguationData":[TD([[makeQuery(id+"F0.imprint","IMPRINT",EDGE,{"disambiguationData":[TD([[subQ2,-1.0]])],"derivedFrom":subQ1}),-1.0]])]});}
            var Q14;
            {var subQ0=sQuery(id+"F0.wireOp",EDGE,"E3.1.0.15");var subQ1=sQuery(id+"F0.wireOp",EDGE,"E3.1.0.12");var subQ2=makeQuery(id+"F0.imprint","INTERSECT",VERTEX,{"derivedFrom":[subQ1,subQ0]});Q14=makeQuery(id+"F0.imprint","IMPRINT",FACE,{"disambiguationData":[TD([[makeQuery(id+"F0.imprint","IMPRINT",EDGE,{"disambiguationData":[TD([[subQ2,-1.0]])],"derivedFrom":subQ1}),1.0]])]});}
            var Q15;
            {var subQ0=sQuery(id+"F0.wireOp",EDGE,"E3.1.0.16");var subQ1=sQuery(id+"F0.wireOp",EDGE,"E3.1.0.12");var subQ2=makeQuery(id+"F0.imprint","INTERSECT",VERTEX,{"derivedFrom":[subQ1,subQ0]});Q15=makeQuery(id+"F0.imprint","IMPRINT",FACE,{"disambiguationData":[TD([[makeQuery(id+"F0.imprint","IMPRINT",EDGE,{"disambiguationData":[TD([[subQ2,-1.0]])],"derivedFrom":subQ1}),1.0]])]});}
            var Q16;
            {var subQ0=sQuery(id+"F0.wireOp",EDGE,"E3.1.0.12");var subQ1=sQuery(id+"F0.wireOp",EDGE,"E3.1.0.4");var subQ2=makeQuery(id+"F0.imprint","INTERSECT",VERTEX,{"derivedFrom":[subQ1,subQ0]});Q16=makeQuery(id+"F0.imprint","IMPRINT",FACE,{"disambiguationData":[TD([[makeQuery(id+"F0.imprint","IMPRINT",EDGE,{"disambiguationData":[TD([[subQ2,-1.0]])],"derivedFrom":subQ1}),-1.0]])]});}
            var Q17;
            {var subQ0=sQuery(id+"F0.wireOp",EDGE,"E25.trimOffspring");var subQ1=sQuery(id+"F0.wireOp",EDGE,"E3.1.0.0");var subQ2=makeQuery(id+"F0.imprint","INTERSECT",VERTEX,{"derivedFrom":[subQ1,subQ0]});Q17=makeQuery(id+"F0.imprint","IMPRINT",FACE,{"disambiguationData":[TD([[makeQuery(id+"F0.imprint","IMPRINT",EDGE,{"disambiguationData":[TD([[subQ2,-1.0]])],"derivedFrom":subQ1}),1.0]])]});}
            var Q18;
            {var subQ0=sQuery(id+"F0.wireOp",EDGE,"E3.1.0.6");var subQ1=sQuery(id+"F0.wireOp",EDGE,"E3.1.0.0");var subQ2=makeQuery(id+"F0.imprint","INTERSECT",VERTEX,{"derivedFrom":[subQ1,subQ0]});Q18=makeQuery(id+"F0.imprint","IMPRINT",FACE,{"disambiguationData":[TD([[makeQuery(id+"F0.imprint","IMPRINT",EDGE,{"disambiguationData":[TD([[subQ2,-1.0]])],"derivedFrom":subQ1}),1.0]])]});}
            var Q19;
            {var subQ0=sQuery(id+"F0.wireOp",EDGE,"E3.1.0.4");var subQ1=sQuery(id+"F0.wireOp",EDGE,"E3.1.0.0");var subQ2=makeQuery(id+"F0.imprint","INTERSECT",VERTEX,{"derivedFrom":[subQ1,subQ0]});Q19=makeQuery(id+"F0.imprint","IMPRINT",FACE,{"disambiguationData":[TD([[makeQuery(id+"F0.imprint","IMPRINT",EDGE,{"disambiguationData":[TD([[subQ2,-1.0]])],"derivedFrom":subQ1}),1.0]])]});}
            var Q20;
            {var subQ0=sQuery(id+"F0.wireOp",EDGE,"E3.1.0.15");var subQ1=sQuery(id+"F0.wireOp",EDGE,"E3.1.0.0");var subQ2=makeQuery(id+"F0.imprint","INTERSECT",VERTEX,{"derivedFrom":[subQ1,subQ0]});Q20=makeQuery(id+"F0.imprint","IMPRINT",FACE,{"disambiguationData":[TD([[makeQuery(id+"F0.imprint","IMPRINT",EDGE,{"disambiguationData":[TD([[subQ2,-1.0]])],"derivedFrom":subQ1}),1.0]])]});}
            var Q21;
            {var subQ0=sQuery(id+"F0.wireOp",EDGE,"E3.1.0.7");var subQ1=sQuery(id+"F0.wireOp",EDGE,"E3.1.0.0");var subQ2=makeQuery(id+"F0.imprint","INTERSECT",VERTEX,{"derivedFrom":[subQ1,subQ0]});Q21=makeQuery(id+"F0.imprint","IMPRINT",FACE,{"disambiguationData":[TD([[makeQuery(id+"F0.imprint","IMPRINT",EDGE,{"disambiguationData":[TD([[subQ2,-1.0]])],"derivedFrom":subQ1}),1.0]])]});}
            var Q22;
            {var subQ0=sQuery(id+"F0.wireOp",EDGE,"E2.0.7.0");var subQ1=sQuery(id+"F0.wireOp",EDGE,"E0.right");var subQ2=makeQuery(id+"F0.imprint","INTERSECT",VERTEX,{"derivedFrom":[subQ1,subQ0]});Q22=makeQuery(id+"F0.imprint","IMPRINT",FACE,{"disambiguationData":[TD([[makeQuery(id+"F0.imprint","IMPRINT",EDGE,{"disambiguationData":[TD([[subQ2,-1.0]])],"derivedFrom":subQ1}),-1.0]])]});}
            var Q23;
            {var subQ0=sQuery(id+"F0.wireOp",EDGE,"E2.0.5.0");var subQ1=sQuery(id+"F0.wireOp",EDGE,"E0.right");var subQ2=makeQuery(id+"F0.imprint","INTERSECT",VERTEX,{"derivedFrom":[subQ1,subQ0]});Q23=makeQuery(id+"F0.imprint","IMPRINT",FACE,{"disambiguationData":[TD([[makeQuery(id+"F0.imprint","IMPRINT",EDGE,{"disambiguationData":[TD([[subQ2,-1.0]])],"derivedFrom":subQ1}),-1.0]])]});}
            var Q24;
            {var subQ0=sQuery(id+"F0.wireOp",EDGE,"E2.0.6.0");var subQ1=sQuery(id+"F0.wireOp",EDGE,"E0.right");var subQ2=makeQuery(id+"F0.imprint","INTERSECT",VERTEX,{"derivedFrom":[subQ1,subQ0]});Q24=makeQuery(id+"F0.imprint","IMPRINT",FACE,{"disambiguationData":[TD([[makeQuery(id+"F0.imprint","IMPRINT",EDGE,{"disambiguationData":[TD([[subQ2,-1.0]])],"derivedFrom":subQ1}),-1.0]])]});}
            var Q25;
            {var subQ0=sQuery(id+"F0.wireOp",EDGE,"E0.right");var subQ1=sQuery(id+"F0.wireOp",EDGE,"E0.top");var subQ2=makeQuery(id+"F0.imprint","INTERSECT",VERTEX,{"derivedFrom":[subQ1,subQ0]});Q25=makeQuery(id+"F0.imprint","IMPRINT",FACE,{"disambiguationData":[TD([[makeQuery(id+"F0.imprint","IMPRINT",EDGE,{"disambiguationData":[TD([[subQ2,1.0]])],"derivedFrom":subQ1}),1.0]])]});}
            var Q26;
            {var subQ0=sQuery(id+"F0.wireOp",EDGE,"E1.5.0.0");var subQ1=sQuery(id+"F0.wireOp",EDGE,"E0.top");var subQ2=makeQuery(id+"F0.imprint","INTERSECT",VERTEX,{"derivedFrom":[subQ1,subQ0]});Q26=makeQuery(id+"F0.imprint","IMPRINT",FACE,{"disambiguationData":[TD([[makeQuery(id+"F0.imprint","IMPRINT",EDGE,{"disambiguationData":[TD([[subQ2,-1.0]])],"derivedFrom":subQ1}),1.0]])]});}
            var Q27;
            {var subQ0=sQuery(id+"F0.wireOp",EDGE,"E1.6.0.0");var subQ1=sQuery(id+"F0.wireOp",EDGE,"E0.top");var subQ2=makeQuery(id+"F0.imprint","INTERSECT",VERTEX,{"derivedFrom":[subQ1,subQ0]});Q27=makeQuery(id+"F0.imprint","IMPRINT",FACE,{"disambiguationData":[TD([[makeQuery(id+"F0.imprint","IMPRINT",EDGE,{"disambiguationData":[TD([[subQ2,-1.0]])],"derivedFrom":subQ1}),1.0]])]});}
            var Q28;
            {var subQ0=sQuery(id+"F0.wireOp",EDGE,"E1.7.0.0");var subQ1=sQuery(id+"F0.wireOp",EDGE,"E0.top");var subQ2=makeQuery(id+"F0.imprint","INTERSECT",VERTEX,{"derivedFrom":[subQ1,subQ0]});Q28=makeQuery(id+"F0.imprint","IMPRINT",FACE,{"disambiguationData":[TD([[makeQuery(id+"F0.imprint","IMPRINT",EDGE,{"disambiguationData":[TD([[subQ2,-1.0]])],"derivedFrom":subQ1}),1.0]])]});}
            var Q29;
            {var subQ0=sQuery(id+"F0.wireOp",EDGE,"E1.1.0.0");var subQ1=sQuery(id+"F0.wireOp",EDGE,"E0.top");var subQ2=makeQuery(id+"F0.imprint","INTERSECT",VERTEX,{"derivedFrom":[subQ1,subQ0]});Q29=makeQuery(id+"F0.imprint","IMPRINT",FACE,{"disambiguationData":[TD([[makeQuery(id+"F0.imprint","IMPRINT",EDGE,{"disambiguationData":[TD([[subQ2,-1.0]])],"derivedFrom":subQ1}),1.0]])]});}
            var Q30;
            {var subQ0=sQuery(id+"F0.wireOp",EDGE,"E1.2.0.0");var subQ1=sQuery(id+"F0.wireOp",EDGE,"E0.top");var subQ2=makeQuery(id+"F0.imprint","INTERSECT",VERTEX,{"derivedFrom":[subQ1,subQ0]});Q30=makeQuery(id+"F0.imprint","IMPRINT",FACE,{"disambiguationData":[TD([[makeQuery(id+"F0.imprint","IMPRINT",EDGE,{"disambiguationData":[TD([[subQ2,-1.0]])],"derivedFrom":subQ1}),1.0]])]});}
            var Q31;
            {var subQ0=sQuery(id+"F0.wireOp",EDGE,"E1.3.0.0");var subQ1=sQuery(id+"F0.wireOp",EDGE,"E0.top");var subQ2=makeQuery(id+"F0.imprint","INTERSECT",VERTEX,{"derivedFrom":[subQ1,subQ0]});Q31=makeQuery(id+"F0.imprint","IMPRINT",FACE,{"disambiguationData":[TD([[makeQuery(id+"F0.imprint","IMPRINT",EDGE,{"disambiguationData":[TD([[subQ2,-1.0]])],"derivedFrom":subQ1}),1.0]])]});}
            var Q32;
            {var subQ0=sQuery(id+"F0.wireOp",EDGE,"E1.4.0.0");var subQ1=sQuery(id+"F0.wireOp",EDGE,"E0.top");var subQ2=makeQuery(id+"F0.imprint","INTERSECT",VERTEX,{"derivedFrom":[subQ1,subQ0]});Q32=makeQuery(id+"F0.imprint","IMPRINT",FACE,{"disambiguationData":[TD([[makeQuery(id+"F0.imprint","IMPRINT",EDGE,{"disambiguationData":[TD([[subQ2,-1.0]])],"derivedFrom":subQ1}),1.0]])]});}
            var Q33;
            {var subQ0=sQuery(id+"F0.wireOp",EDGE,"E0.left");var subQ1=sQuery(id+"F0.wireOp",EDGE,"E0.top");var subQ2=makeQuery(id+"F0.imprint","INTERSECT",VERTEX,{"derivedFrom":[subQ1,subQ0]});Q33=makeQuery(id+"F0.imprint","IMPRINT",FACE,{"disambiguationData":[TD([[makeQuery(id+"F0.imprint","IMPRINT",EDGE,{"disambiguationData":[TD([[subQ2,-1.0]])],"derivedFrom":subQ1}),1.0]])]});}
            var Q34;
            {var subQ0=sQuery(id+"F0.wireOp",EDGE,"E2.0.6.0");var subQ1=sQuery(id+"F0.wireOp",EDGE,"E1.3.0.0");var subQ2=makeQuery(id+"F0.imprint","INTERSECT",VERTEX,{"derivedFrom":[subQ1,subQ0]});Q34=makeQuery(id+"F0.imprint","IMPRINT",FACE,{"disambiguationData":[TD([[makeQuery(id+"F0.imprint","IMPRINT",EDGE,{"disambiguationData":[TD([[subQ2,-1.0]])],"derivedFrom":subQ1}),1.0]])]});}
            var Q35;
            {var subQ0=sQuery(id+"F0.wireOp",EDGE,"E2.0.6.0");var subQ1=sQuery(id+"F0.wireOp",EDGE,"E0.left");var subQ2=makeQuery(id+"F0.imprint","INTERSECT",VERTEX,{"derivedFrom":[subQ1,subQ0]});Q35=makeQuery(id+"F0.imprint","IMPRINT",FACE,{"disambiguationData":[TD([[makeQuery(id+"F0.imprint","IMPRINT",EDGE,{"disambiguationData":[TD([[subQ2,-1.0]])],"derivedFrom":subQ1}),1.0]])]});}
            var Q36;
            {var subQ0=sQuery(id+"F0.wireOp",EDGE,"E2.0.6.0");var subQ1=sQuery(id+"F0.wireOp",EDGE,"E1.1.0.0");var subQ2=makeQuery(id+"F0.imprint","INTERSECT",VERTEX,{"derivedFrom":[subQ1,subQ0]});Q36=makeQuery(id+"F0.imprint","IMPRINT",FACE,{"disambiguationData":[TD([[makeQuery(id+"F0.imprint","IMPRINT",EDGE,{"disambiguationData":[TD([[subQ2,-1.0]])],"derivedFrom":subQ1}),1.0]])]});}
            var Q37;
            {var subQ0=sQuery(id+"F0.wireOp",EDGE,"E2.0.6.0");var subQ1=sQuery(id+"F0.wireOp",EDGE,"E1.6.0.0");var subQ2=makeQuery(id+"F0.imprint","INTERSECT",VERTEX,{"derivedFrom":[subQ1,subQ0]});Q37=makeQuery(id+"F0.imprint","IMPRINT",FACE,{"disambiguationData":[TD([[makeQuery(id+"F0.imprint","IMPRINT",EDGE,{"disambiguationData":[TD([[subQ2,-1.0]])],"derivedFrom":subQ1}),1.0]])]});}
            var Q38;
            {var subQ0=sQuery(id+"F0.wireOp",EDGE,"E2.0.6.0");var subQ1=sQuery(id+"F0.wireOp",EDGE,"E1.5.0.0");var subQ2=makeQuery(id+"F0.imprint","INTERSECT",VERTEX,{"derivedFrom":[subQ1,subQ0]});Q38=makeQuery(id+"F0.imprint","IMPRINT",FACE,{"disambiguationData":[TD([[makeQuery(id+"F0.imprint","IMPRINT",EDGE,{"disambiguationData":[TD([[subQ2,-1.0]])],"derivedFrom":subQ1}),1.0]])]});}
            var Q39;
            {var subQ0=sQuery(id+"F0.wireOp",EDGE,"E2.0.6.0");var subQ1=sQuery(id+"F0.wireOp",EDGE,"E1.2.0.0");var subQ2=makeQuery(id+"F0.imprint","INTERSECT",VERTEX,{"derivedFrom":[subQ1,subQ0]});Q39=makeQuery(id+"F0.imprint","IMPRINT",FACE,{"disambiguationData":[TD([[makeQuery(id+"F0.imprint","IMPRINT",EDGE,{"disambiguationData":[TD([[subQ2,-1.0]])],"derivedFrom":subQ1}),1.0]])]});}
            var Q40;
            {var subQ0=sQuery(id+"F0.wireOp",EDGE,"E2.0.6.0");var subQ1=sQuery(id+"F0.wireOp",EDGE,"E1.4.0.0");var subQ2=makeQuery(id+"F0.imprint","INTERSECT",VERTEX,{"derivedFrom":[subQ1,subQ0]});Q40=makeQuery(id+"F0.imprint","IMPRINT",FACE,{"disambiguationData":[TD([[makeQuery(id+"F0.imprint","IMPRINT",EDGE,{"disambiguationData":[TD([[subQ2,-1.0]])],"derivedFrom":subQ1}),1.0]])]});}
            var Q41;
            {var subQ0=sQuery(id+"F0.wireOp",EDGE,"E3.0.1.7");var subQ1=sQuery(id+"F0.wireOp",EDGE,"E3.0.1.1");var subQ2=makeQuery(id+"F0.imprint","INTERSECT",VERTEX,{"derivedFrom":[subQ1,subQ0]});Q41=makeQuery(id+"F0.imprint","IMPRINT",FACE,{"disambiguationData":[TD([[makeQuery(id+"F0.imprint","IMPRINT",EDGE,{"disambiguationData":[TD([[subQ2,-1.0]])],"derivedFrom":subQ1}),-1.0]])]});}
            var Q42;
            {var subQ0=sQuery(id+"F0.wireOp",EDGE,"E3.0.1.10");var subQ1=sQuery(id+"F0.wireOp",EDGE,"E3.0.1.3");var subQ2=makeQuery(id+"F0.imprint","INTERSECT",VERTEX,{"derivedFrom":[subQ1,subQ0]});Q42=makeQuery(id+"F0.imprint","IMPRINT",FACE,{"disambiguationData":[TD([[makeQuery(id+"F0.imprint","IMPRINT",EDGE,{"disambiguationData":[TD([[subQ2,1.0]])],"derivedFrom":subQ1}),1.0]])]});}
            var Q43;
            {var subQ0=sQuery(id+"F0.wireOp",EDGE,"E3.0.1.11");var subQ1=sQuery(id+"F0.wireOp",EDGE,"E3.0.1.3");var subQ2=makeQuery(id+"F0.imprint","INTERSECT",VERTEX,{"derivedFrom":[subQ1,subQ0]});Q43=makeQuery(id+"F0.imprint","IMPRINT",FACE,{"disambiguationData":[TD([[makeQuery(id+"F0.imprint","IMPRINT",EDGE,{"disambiguationData":[TD([[subQ2,-1.0]])],"derivedFrom":subQ1}),1.0]])]});}
            var Q44;
            {var subQ0=sQuery(id+"F0.wireOp",EDGE,"E3.0.1.12");var subQ1=sQuery(id+"F0.wireOp",EDGE,"E3.0.1.3");var subQ2=makeQuery(id+"F0.imprint","INTERSECT",VERTEX,{"derivedFrom":[subQ1,subQ0]});Q44=makeQuery(id+"F0.imprint","IMPRINT",FACE,{"disambiguationData":[TD([[makeQuery(id+"F0.imprint","IMPRINT",EDGE,{"disambiguationData":[TD([[subQ2,-1.0]])],"derivedFrom":subQ1}),1.0]])]});}
            var Q45;
            {var subQ0=sQuery(id+"F0.wireOp",EDGE,"E3.0.1.7");var subQ1=sQuery(id+"F0.wireOp",EDGE,"E3.0.1.0");var subQ2=makeQuery(id+"F0.imprint","INTERSECT",VERTEX,{"derivedFrom":[subQ1,subQ0]});Q45=makeQuery(id+"F0.imprint","IMPRINT",FACE,{"disambiguationData":[TD([[makeQuery(id+"F0.imprint","IMPRINT",EDGE,{"disambiguationData":[TD([[subQ2,-1.0]])],"derivedFrom":subQ1}),-1.0]])]});}
            var Q46;
            {var subQ0=sQuery(id+"F0.wireOp",EDGE,"E3.0.1.13");var subQ1=sQuery(id+"F0.wireOp",EDGE,"E3.0.1.3");var subQ2=makeQuery(id+"F0.imprint","INTERSECT",VERTEX,{"derivedFrom":[subQ1,subQ0]});Q46=makeQuery(id+"F0.imprint","IMPRINT",FACE,{"disambiguationData":[TD([[makeQuery(id+"F0.imprint","IMPRINT",EDGE,{"disambiguationData":[TD([[subQ2,-1.0]])],"derivedFrom":subQ1}),1.0]])]});}
            var Q47;
            {var subQ0=sQuery(id+"F0.wireOp",EDGE,"E3.0.1.7");var subQ1=sQuery(id+"F0.wireOp",EDGE,"E3.0.1.0");var subQ2=makeQuery(id+"F0.imprint","INTERSECT",VERTEX,{"derivedFrom":[subQ1,subQ0]});Q47=makeQuery(id+"F0.imprint","IMPRINT",FACE,{"disambiguationData":[TD([[makeQuery(id+"F0.imprint","IMPRINT",EDGE,{"disambiguationData":[TD([[subQ2,-1.0]])],"derivedFrom":subQ1}),1.0]])]});}
            var Q48;
            {var subQ0=sQuery(id+"F0.wireOp",EDGE,"E3.0.1.7");var subQ1=sQuery(id+"F0.wireOp",EDGE,"E3.0.1.1");var subQ2=makeQuery(id+"F0.imprint","INTERSECT",VERTEX,{"derivedFrom":[subQ1,subQ0]});Q48=makeQuery(id+"F0.imprint","IMPRINT",FACE,{"disambiguationData":[TD([[makeQuery(id+"F0.imprint","IMPRINT",EDGE,{"disambiguationData":[TD([[subQ2,-1.0]])],"derivedFrom":subQ1}),1.0]])]});}
            var Q49;
            {var subQ0=sQuery(id+"F0.wireOp",EDGE,"E3.0.1.7");var subQ1=sQuery(id+"F0.wireOp",EDGE,"E3.0.1.2");var subQ2=makeQuery(id+"F0.imprint","INTERSECT",VERTEX,{"derivedFrom":[subQ1,subQ0]});Q49=makeQuery(id+"F0.imprint","IMPRINT",FACE,{"disambiguationData":[TD([[makeQuery(id+"F0.imprint","IMPRINT",EDGE,{"disambiguationData":[TD([[subQ2,-1.0]])],"derivedFrom":subQ1}),-1.0]])]});}
            var Q50;
            {var subQ0=sQuery(id+"F0.wireOp",EDGE,"E3.0.1.8");var subQ1=sQuery(id+"F0.wireOp",EDGE,"E3.0.1.0");var subQ2=makeQuery(id+"F0.imprint","INTERSECT",VERTEX,{"derivedFrom":[subQ1,subQ0]});Q50=makeQuery(id+"F0.imprint","IMPRINT",FACE,{"disambiguationData":[TD([[makeQuery(id+"F0.imprint","IMPRINT",EDGE,{"disambiguationData":[TD([[subQ2,1.0]])],"derivedFrom":subQ1}),1.0]])]});}
            var Q51;
            {var subQ0=sQuery(id+"F0.wireOp",EDGE,"E3.0.1.4");var subQ1=sQuery(id+"F0.wireOp",EDGE,"E3.0.1.0");var subQ2=makeQuery(id+"F0.imprint","INTERSECT",VERTEX,{"derivedFrom":[subQ1,subQ0]});Q51=makeQuery(id+"F0.imprint","IMPRINT",FACE,{"disambiguationData":[TD([[makeQuery(id+"F0.imprint","IMPRINT",EDGE,{"disambiguationData":[TD([[subQ2,-1.0]])],"derivedFrom":subQ1}),1.0]])]});}
            var Q52;
            {var subQ0=sQuery(id+"F0.wireOp",EDGE,"E3.0.1.6");var subQ1=sQuery(id+"F0.wireOp",EDGE,"E3.0.1.0");var subQ2=makeQuery(id+"F0.imprint","INTERSECT",VERTEX,{"derivedFrom":[subQ1,subQ0]});Q52=makeQuery(id+"F0.imprint","IMPRINT",FACE,{"disambiguationData":[TD([[makeQuery(id+"F0.imprint","IMPRINT",EDGE,{"disambiguationData":[TD([[subQ2,-1.0]])],"derivedFrom":subQ1}),1.0]])]});}
            var Q53;
            {var subQ0=sQuery(id+"F0.wireOp",EDGE,"E3.0.1.15");var subQ1=sQuery(id+"F0.wireOp",EDGE,"E3.0.1.0");var subQ2=makeQuery(id+"F0.imprint","INTERSECT",VERTEX,{"derivedFrom":[subQ1,subQ0]});Q53=makeQuery(id+"F0.imprint","IMPRINT",FACE,{"disambiguationData":[TD([[makeQuery(id+"F0.imprint","IMPRINT",EDGE,{"disambiguationData":[TD([[subQ2,-1.0]])],"derivedFrom":subQ1}),1.0]])]});}
            var Q54;
            {var subQ0=sQuery(id+"F0.wireOp",EDGE,"E3.0.1.16");var subQ1=sQuery(id+"F0.wireOp",EDGE,"E3.0.1.0");var subQ2=makeQuery(id+"F0.imprint","INTERSECT",VERTEX,{"derivedFrom":[subQ1,subQ0]});Q54=makeQuery(id+"F0.imprint","IMPRINT",FACE,{"disambiguationData":[TD([[makeQuery(id+"F0.imprint","IMPRINT",EDGE,{"disambiguationData":[TD([[subQ2,-1.0]])],"derivedFrom":subQ1}),1.0]])]});}
            var Q55;
            {var subQ0=sQuery(id+"F0.wireOp",EDGE,"E3.0.1.19");var subQ1=sQuery(id+"F0.wireOp",EDGE,"E3.0.1.0");var subQ2=makeQuery(id+"F0.imprint","INTERSECT",VERTEX,{"derivedFrom":[subQ1,subQ0]});Q55=makeQuery(id+"F0.imprint","IMPRINT",FACE,{"disambiguationData":[TD([[makeQuery(id+"F0.imprint","IMPRINT",EDGE,{"disambiguationData":[TD([[subQ2,-1.0]])],"derivedFrom":subQ1}),1.0]])]});}
            var Q56;
            {var subQ0=sQuery(id+"F0.wireOp",EDGE,"E3.0.1.3");var subQ1=sQuery(id+"F0.wireOp",EDGE,"E3.0.1.0");var subQ2=makeQuery(id+"F0.imprint","INTERSECT",VERTEX,{"derivedFrom":[subQ1,subQ0]});Q56=makeQuery(id+"F0.imprint","IMPRINT",FACE,{"disambiguationData":[TD([[makeQuery(id+"F0.imprint","IMPRINT",EDGE,{"disambiguationData":[TD([[subQ2,-1.0]])],"derivedFrom":subQ1}),1.0]])]});}
            var Q57;
            {var subQ0=sQuery(id+"F0.wireOp",EDGE,"E3.0.1.20");var subQ1=sQuery(id+"F0.wireOp",EDGE,"E3.0.1.0");var subQ2=makeQuery(id+"F0.imprint","INTERSECT",VERTEX,{"derivedFrom":[subQ1,subQ0]});Q57=makeQuery(id+"F0.imprint","IMPRINT",FACE,{"disambiguationData":[TD([[makeQuery(id+"F0.imprint","IMPRINT",EDGE,{"disambiguationData":[TD([[subQ2,-1.0]])],"derivedFrom":subQ1}),1.0]])]});}
            var Q58;
            {var subQ0=sQuery(id+"F0.wireOp",EDGE,"E3.0.1.13");var subQ1=sQuery(id+"F0.wireOp",EDGE,"E3.0.1.4");var subQ2=makeQuery(id+"F0.imprint","INTERSECT",VERTEX,{"derivedFrom":[subQ1,subQ0]});Q58=makeQuery(id+"F0.imprint","IMPRINT",FACE,{"disambiguationData":[TD([[makeQuery(id+"F0.imprint","IMPRINT",EDGE,{"disambiguationData":[TD([[subQ2,-1.0]])],"derivedFrom":subQ1}),-1.0]])]});}
            var Q59;
            {var subQ0=sQuery(id+"F0.wireOp",EDGE,"E3.0.1.10");var subQ1=sQuery(id+"F0.wireOp",EDGE,"E3.0.1.4");var subQ2=makeQuery(id+"F0.imprint","INTERSECT",VERTEX,{"derivedFrom":[subQ1,subQ0]});Q59=makeQuery(id+"F0.imprint","IMPRINT",FACE,{"disambiguationData":[TD([[makeQuery(id+"F0.imprint","IMPRINT",EDGE,{"disambiguationData":[TD([[subQ2,1.0]])],"derivedFrom":subQ1}),-1.0]])]});}
            var Q60;
            {var subQ0=sQuery(id+"F0.wireOp",EDGE,"E3.0.1.12");var subQ1=sQuery(id+"F0.wireOp",EDGE,"E3.0.1.4");var subQ2=makeQuery(id+"F0.imprint","INTERSECT",VERTEX,{"derivedFrom":[subQ1,subQ0]});Q60=makeQuery(id+"F0.imprint","IMPRINT",FACE,{"disambiguationData":[TD([[makeQuery(id+"F0.imprint","IMPRINT",EDGE,{"disambiguationData":[TD([[subQ2,-1.0]])],"derivedFrom":subQ1}),-1.0]])]});}
            var Q61;
            {var subQ0=sQuery(id+"F0.wireOp",EDGE,"E3.0.1.12");var subQ1=sQuery(id+"F0.wireOp",EDGE,"E3.0.1.6");var subQ2=makeQuery(id+"F0.imprint","INTERSECT",VERTEX,{"derivedFrom":[subQ1,subQ0]});Q61=makeQuery(id+"F0.imprint","IMPRINT",FACE,{"disambiguationData":[TD([[makeQuery(id+"F0.imprint","IMPRINT",EDGE,{"disambiguationData":[TD([[subQ2,-1.0]])],"derivedFrom":subQ1}),-1.0]])]});}
            var Q62;
            {var subQ0=sQuery(id+"F0.wireOp",EDGE,"E3.0.1.12");var subQ1=sQuery(id+"F0.wireOp",EDGE,"E3.0.1.8");var subQ2=makeQuery(id+"F0.imprint","INTERSECT",VERTEX,{"derivedFrom":[subQ1,subQ0]});Q62=makeQuery(id+"F0.imprint","IMPRINT",FACE,{"disambiguationData":[TD([[makeQuery(id+"F0.imprint","IMPRINT",EDGE,{"disambiguationData":[TD([[subQ2,-1.0]])],"derivedFrom":subQ1}),1.0]])]});}
            var Q63;
            {var subQ0=sQuery(id+"F0.wireOp",EDGE,"E3.0.1.15");var subQ1=sQuery(id+"F0.wireOp",EDGE,"E3.0.1.12");var subQ2=makeQuery(id+"F0.imprint","INTERSECT",VERTEX,{"derivedFrom":[subQ1,subQ0]});Q63=makeQuery(id+"F0.imprint","IMPRINT",FACE,{"disambiguationData":[TD([[makeQuery(id+"F0.imprint","IMPRINT",EDGE,{"disambiguationData":[TD([[subQ2,-1.0]])],"derivedFrom":subQ1}),1.0]])]});}
            var Q64;
            {var subQ0=sQuery(id+"F0.wireOp",EDGE,"E3.0.1.16");var subQ1=sQuery(id+"F0.wireOp",EDGE,"E3.0.1.12");var subQ2=makeQuery(id+"F0.imprint","INTERSECT",VERTEX,{"derivedFrom":[subQ1,subQ0]});Q64=makeQuery(id+"F0.imprint","IMPRINT",FACE,{"disambiguationData":[TD([[makeQuery(id+"F0.imprint","IMPRINT",EDGE,{"disambiguationData":[TD([[subQ2,-1.0]])],"derivedFrom":subQ1}),1.0]])]});}
            var Q65;
            {var subQ0=sQuery(id+"F0.wireOp",EDGE,"E3.0.1.19");var subQ1=sQuery(id+"F0.wireOp",EDGE,"E3.0.1.12");var subQ2=makeQuery(id+"F0.imprint","INTERSECT",VERTEX,{"derivedFrom":[subQ1,subQ0]});Q65=makeQuery(id+"F0.imprint","IMPRINT",FACE,{"disambiguationData":[TD([[makeQuery(id+"F0.imprint","IMPRINT",EDGE,{"disambiguationData":[TD([[subQ2,-1.0]])],"derivedFrom":subQ1}),1.0]])]});}
            var Q66;
            {var subQ0=sQuery(id+"F0.wireOp",EDGE,"E3.0.1.20");var subQ1=sQuery(id+"F0.wireOp",EDGE,"E3.0.1.12");var subQ2=makeQuery(id+"F0.imprint","INTERSECT",VERTEX,{"derivedFrom":[subQ1,subQ0]});Q66=makeQuery(id+"F0.imprint","IMPRINT",FACE,{"disambiguationData":[TD([[makeQuery(id+"F0.imprint","IMPRINT",EDGE,{"disambiguationData":[TD([[subQ2,-1.0]])],"derivedFrom":subQ1}),1.0]])]});}
            var Q67;
            {var subQ0=sQuery(id+"F0.wireOp",EDGE,"E3.0.1.10");var subQ1=sQuery(id+"F0.wireOp",EDGE,"E3.0.1.8");var subQ2=makeQuery(id+"F0.imprint","INTERSECT",VERTEX,{"derivedFrom":[subQ1,subQ0]});Q67=makeQuery(id+"F0.imprint","IMPRINT",FACE,{"disambiguationData":[TD([[makeQuery(id+"F0.imprint","IMPRINT",EDGE,{"disambiguationData":[TD([[subQ2,1.0]])],"derivedFrom":subQ1}),1.0]])]});}
            var Q68;
            {var subQ0=sQuery(id+"F0.wireOp",EDGE,"E3.0.1.15");var subQ1=sQuery(id+"F0.wireOp",EDGE,"E3.0.1.10");var subQ2=makeQuery(id+"F0.imprint","INTERSECT",VERTEX,{"derivedFrom":[subQ1,subQ0]});Q68=makeQuery(id+"F0.imprint","IMPRINT",FACE,{"disambiguationData":[TD([[makeQuery(id+"F0.imprint","IMPRINT",EDGE,{"disambiguationData":[TD([[subQ2,-1.0]])],"derivedFrom":subQ1}),-1.0]])]});}
            var Q69;
            {var subQ0=sQuery(id+"F0.wireOp",EDGE,"E3.0.1.16");var subQ1=sQuery(id+"F0.wireOp",EDGE,"E3.0.1.10");var subQ2=makeQuery(id+"F0.imprint","INTERSECT",VERTEX,{"derivedFrom":[subQ1,subQ0]});Q69=makeQuery(id+"F0.imprint","IMPRINT",FACE,{"disambiguationData":[TD([[makeQuery(id+"F0.imprint","IMPRINT",EDGE,{"disambiguationData":[TD([[subQ2,-1.0]])],"derivedFrom":subQ1}),-1.0]])]});}
            var Q70;
            {var subQ0=sQuery(id+"F0.wireOp",EDGE,"E3.0.1.19");var subQ1=sQuery(id+"F0.wireOp",EDGE,"E3.0.1.10");var subQ2=makeQuery(id+"F0.imprint","INTERSECT",VERTEX,{"derivedFrom":[subQ1,subQ0]});Q70=makeQuery(id+"F0.imprint","IMPRINT",FACE,{"disambiguationData":[TD([[makeQuery(id+"F0.imprint","IMPRINT",EDGE,{"disambiguationData":[TD([[subQ2,-1.0]])],"derivedFrom":subQ1}),-1.0]])]});}
            var Q71;
            {var subQ0=sQuery(id+"F0.wireOp",EDGE,"E3.0.1.18");var subQ1=sQuery(id+"F0.wireOp",EDGE,"E3.0.1.10");var subQ2=makeQuery(id+"F0.imprint","INTERSECT",VERTEX,{"derivedFrom":[subQ1,subQ0]});Q71=makeQuery(id+"F0.imprint","IMPRINT",FACE,{"disambiguationData":[TD([[makeQuery(id+"F0.imprint","IMPRINT",EDGE,{"disambiguationData":[TD([[subQ2,1.0]])],"derivedFrom":subQ1}),-1.0]])]});}
            var Q72;
            {var subQ0=sQuery(id+"F0.wireOp",EDGE,"E3.0.1.4");var subQ1=sQuery(id+"F0.wireOp",EDGE,"E3.0.1.1");var subQ2=makeQuery(id+"F0.imprint","INTERSECT",VERTEX,{"derivedFrom":[subQ1,subQ0]});Q72=makeQuery(id+"F0.imprint","IMPRINT",FACE,{"disambiguationData":[TD([[makeQuery(id+"F0.imprint","IMPRINT",EDGE,{"disambiguationData":[TD([[subQ2,-1.0]])],"derivedFrom":subQ1}),1.0]])]});}
            var Q73;
            {var subQ0=sQuery(id+"F0.wireOp",EDGE,"E3.0.1.4");var subQ1=sQuery(id+"F0.wireOp",EDGE,"E3.0.1.2");var subQ2=makeQuery(id+"F0.imprint","INTERSECT",VERTEX,{"derivedFrom":[subQ1,subQ0]});Q73=makeQuery(id+"F0.imprint","IMPRINT",FACE,{"disambiguationData":[TD([[makeQuery(id+"F0.imprint","IMPRINT",EDGE,{"disambiguationData":[TD([[subQ2,-1.0]])],"derivedFrom":subQ1}),-1.0]])]});}
            var Q74;
            {var subQ0=sQuery(id+"F0.wireOp",EDGE,"E3.0.1.4");var subQ1=sQuery(id+"F0.wireOp",EDGE,"E3.0.1.1");var subQ2=makeQuery(id+"F0.imprint","INTERSECT",VERTEX,{"derivedFrom":[subQ1,subQ0]});Q74=makeQuery(id+"F0.imprint","IMPRINT",FACE,{"disambiguationData":[TD([[makeQuery(id+"F0.imprint","IMPRINT",EDGE,{"disambiguationData":[TD([[subQ2,-1.0]])],"derivedFrom":subQ1}),-1.0]])]});}
            var Q75;
            {var subQ0=sQuery(id+"F0.wireOp",EDGE,"E3.0.1.6");var subQ1=sQuery(id+"F0.wireOp",EDGE,"E3.0.1.2");var subQ2=makeQuery(id+"F0.imprint","INTERSECT",VERTEX,{"derivedFrom":[subQ1,subQ0]});Q75=makeQuery(id+"F0.imprint","IMPRINT",FACE,{"disambiguationData":[TD([[makeQuery(id+"F0.imprint","IMPRINT",EDGE,{"disambiguationData":[TD([[subQ2,-1.0]])],"derivedFrom":subQ1}),-1.0]])]});}
            var Q76;
            {var subQ0=sQuery(id+"F0.wireOp",EDGE,"E3.0.1.15");var subQ1=sQuery(id+"F0.wireOp",EDGE,"E3.0.1.2");var subQ2=makeQuery(id+"F0.imprint","INTERSECT",VERTEX,{"derivedFrom":[subQ1,subQ0]});Q76=makeQuery(id+"F0.imprint","IMPRINT",FACE,{"disambiguationData":[TD([[makeQuery(id+"F0.imprint","IMPRINT",EDGE,{"disambiguationData":[TD([[subQ2,-1.0]])],"derivedFrom":subQ1}),-1.0]])]});}
            var Q77;
            {var subQ0=sQuery(id+"F0.wireOp",EDGE,"E3.0.1.16");var subQ1=sQuery(id+"F0.wireOp",EDGE,"E3.0.1.2");var subQ2=makeQuery(id+"F0.imprint","INTERSECT",VERTEX,{"derivedFrom":[subQ1,subQ0]});Q77=makeQuery(id+"F0.imprint","IMPRINT",FACE,{"disambiguationData":[TD([[makeQuery(id+"F0.imprint","IMPRINT",EDGE,{"disambiguationData":[TD([[subQ2,-1.0]])],"derivedFrom":subQ1}),-1.0]])]});}
            var Q78;
            {var subQ0=sQuery(id+"F0.wireOp",EDGE,"E3.0.1.19");var subQ1=sQuery(id+"F0.wireOp",EDGE,"E3.0.1.2");var subQ2=makeQuery(id+"F0.imprint","INTERSECT",VERTEX,{"derivedFrom":[subQ1,subQ0]});Q78=makeQuery(id+"F0.imprint","IMPRINT",FACE,{"disambiguationData":[TD([[makeQuery(id+"F0.imprint","IMPRINT",EDGE,{"disambiguationData":[TD([[subQ2,-1.0]])],"derivedFrom":subQ1}),-1.0]])]});}
            var Q79;
            {var subQ0=sQuery(id+"F0.wireOp",EDGE,"E3.0.1.20");var subQ1=sQuery(id+"F0.wireOp",EDGE,"E3.0.1.2");var subQ2=makeQuery(id+"F0.imprint","INTERSECT",VERTEX,{"derivedFrom":[subQ1,subQ0]});Q79=makeQuery(id+"F0.imprint","IMPRINT",FACE,{"disambiguationData":[TD([[makeQuery(id+"F0.imprint","IMPRINT",EDGE,{"disambiguationData":[TD([[subQ2,-1.0]])],"derivedFrom":subQ1}),-1.0]])]});}
            var Q80;
            {var subQ0=sQuery(id+"F0.wireOp",EDGE,"E3.0.1.8");var subQ1=sQuery(id+"F0.wireOp",EDGE,"E3.0.1.2");var subQ2=makeQuery(id+"F0.imprint","INTERSECT",VERTEX,{"derivedFrom":[subQ1,subQ0]});Q80=makeQuery(id+"F0.imprint","IMPRINT",FACE,{"disambiguationData":[TD([[makeQuery(id+"F0.imprint","IMPRINT",EDGE,{"disambiguationData":[TD([[subQ2,1.0]])],"derivedFrom":subQ1}),-1.0]])]});}
            var Q81;
            {var subQ0=sQuery(id+"F0.wireOp",EDGE,"E3.0.1.8");var subQ1=sQuery(id+"F0.wireOp",EDGE,"E3.0.1.1");var subQ2=makeQuery(id+"F0.imprint","INTERSECT",VERTEX,{"derivedFrom":[subQ1,subQ0]});Q81=makeQuery(id+"F0.imprint","IMPRINT",FACE,{"disambiguationData":[TD([[makeQuery(id+"F0.imprint","IMPRINT",EDGE,{"disambiguationData":[TD([[subQ2,1.0]])],"derivedFrom":subQ1}),-1.0]])]});}
            var Q82;
            {var subQ0=sQuery(id+"F0.wireOp",EDGE,"E3.0.1.15");var subQ1=sQuery(id+"F0.wireOp",EDGE,"E3.0.1.1");var subQ2=makeQuery(id+"F0.imprint","INTERSECT",VERTEX,{"derivedFrom":[subQ1,subQ0]});Q82=makeQuery(id+"F0.imprint","IMPRINT",FACE,{"disambiguationData":[TD([[makeQuery(id+"F0.imprint","IMPRINT",EDGE,{"disambiguationData":[TD([[subQ2,-1.0]])],"derivedFrom":subQ1}),-1.0]])]});}
            var Q83;
            {var subQ0=sQuery(id+"F0.wireOp",EDGE,"E3.0.1.16");var subQ1=sQuery(id+"F0.wireOp",EDGE,"E3.0.1.1");var subQ2=makeQuery(id+"F0.imprint","INTERSECT",VERTEX,{"derivedFrom":[subQ1,subQ0]});Q83=makeQuery(id+"F0.imprint","IMPRINT",FACE,{"disambiguationData":[TD([[makeQuery(id+"F0.imprint","IMPRINT",EDGE,{"disambiguationData":[TD([[subQ2,-1.0]])],"derivedFrom":subQ1}),-1.0]])]});}
            var Q84;
            {var subQ0=sQuery(id+"F0.wireOp",EDGE,"E3.0.1.19");var subQ1=sQuery(id+"F0.wireOp",EDGE,"E3.0.1.1");var subQ2=makeQuery(id+"F0.imprint","INTERSECT",VERTEX,{"derivedFrom":[subQ1,subQ0]});Q84=makeQuery(id+"F0.imprint","IMPRINT",FACE,{"disambiguationData":[TD([[makeQuery(id+"F0.imprint","IMPRINT",EDGE,{"disambiguationData":[TD([[subQ2,-1.0]])],"derivedFrom":subQ1}),-1.0]])]});}
            var Q85;
            {var subQ0=sQuery(id+"F0.wireOp",EDGE,"E3.0.1.20");var subQ1=sQuery(id+"F0.wireOp",EDGE,"E3.0.1.1");var subQ2=makeQuery(id+"F0.imprint","INTERSECT",VERTEX,{"derivedFrom":[subQ1,subQ0]});Q85=makeQuery(id+"F0.imprint","IMPRINT",FACE,{"disambiguationData":[TD([[makeQuery(id+"F0.imprint","IMPRINT",EDGE,{"disambiguationData":[TD([[subQ2,-1.0]])],"derivedFrom":subQ1}),-1.0]])]});}
            var Q86;
            {var subQ0=sQuery(id+"F0.wireOp",EDGE,"E3.1.1.7");var subQ1=sQuery(id+"F0.wireOp",EDGE,"E3.1.1.1");var subQ2=makeQuery(id+"F0.imprint","INTERSECT",VERTEX,{"derivedFrom":[subQ1,subQ0]});Q86=makeQuery(id+"F0.imprint","IMPRINT",FACE,{"disambiguationData":[TD([[makeQuery(id+"F0.imprint","IMPRINT",EDGE,{"disambiguationData":[TD([[subQ2,-1.0]])],"derivedFrom":subQ1}),-1.0]])]});}
            var Q87;
            {var subQ0=sQuery(id+"F0.wireOp",EDGE,"E3.1.1.10");var subQ1=sQuery(id+"F0.wireOp",EDGE,"E3.1.1.3");var subQ2=makeQuery(id+"F0.imprint","INTERSECT",VERTEX,{"derivedFrom":[subQ1,subQ0]});Q87=makeQuery(id+"F0.imprint","IMPRINT",FACE,{"disambiguationData":[TD([[makeQuery(id+"F0.imprint","IMPRINT",EDGE,{"disambiguationData":[TD([[subQ2,1.0]])],"derivedFrom":subQ1}),1.0]])]});}
            var Q88;
            {var subQ0=sQuery(id+"F0.wireOp",EDGE,"E3.1.1.7");var subQ1=sQuery(id+"F0.wireOp",EDGE,"E3.1.1.2");var subQ2=makeQuery(id+"F0.imprint","INTERSECT",VERTEX,{"derivedFrom":[subQ1,subQ0]});Q88=makeQuery(id+"F0.imprint","IMPRINT",FACE,{"disambiguationData":[TD([[makeQuery(id+"F0.imprint","IMPRINT",EDGE,{"disambiguationData":[TD([[subQ2,-1.0]])],"derivedFrom":subQ1}),-1.0]])]});}
            var Q89;
            {var subQ0=sQuery(id+"F0.wireOp",EDGE,"E3.1.1.11");var subQ1=sQuery(id+"F0.wireOp",EDGE,"E3.1.1.3");var subQ2=makeQuery(id+"F0.imprint","INTERSECT",VERTEX,{"derivedFrom":[subQ1,subQ0]});Q89=makeQuery(id+"F0.imprint","IMPRINT",FACE,{"disambiguationData":[TD([[makeQuery(id+"F0.imprint","IMPRINT",EDGE,{"disambiguationData":[TD([[subQ2,-1.0]])],"derivedFrom":subQ1}),1.0]])]});}
            var Q90;
            {var subQ0=sQuery(id+"F0.wireOp",EDGE,"E3.1.1.12");var subQ1=sQuery(id+"F0.wireOp",EDGE,"E3.1.1.3");var subQ2=makeQuery(id+"F0.imprint","INTERSECT",VERTEX,{"derivedFrom":[subQ1,subQ0]});Q90=makeQuery(id+"F0.imprint","IMPRINT",FACE,{"disambiguationData":[TD([[makeQuery(id+"F0.imprint","IMPRINT",EDGE,{"disambiguationData":[TD([[subQ2,-1.0]])],"derivedFrom":subQ1}),1.0]])]});}
            var Q91;
            {var subQ0=sQuery(id+"F0.wireOp",EDGE,"E3.1.1.7");var subQ1=sQuery(id+"F0.wireOp",EDGE,"E3.1.1.0");var subQ2=makeQuery(id+"F0.imprint","INTERSECT",VERTEX,{"derivedFrom":[subQ1,subQ0]});Q91=makeQuery(id+"F0.imprint","IMPRINT",FACE,{"disambiguationData":[TD([[makeQuery(id+"F0.imprint","IMPRINT",EDGE,{"disambiguationData":[TD([[subQ2,-1.0]])],"derivedFrom":subQ1}),-1.0]])]});}
            var Q92;
            {var subQ0=sQuery(id+"F0.wireOp",EDGE,"E3.1.1.7");var subQ1=sQuery(id+"F0.wireOp",EDGE,"E3.1.1.0");var subQ2=makeQuery(id+"F0.imprint","INTERSECT",VERTEX,{"derivedFrom":[subQ1,subQ0]});Q92=makeQuery(id+"F0.imprint","IMPRINT",FACE,{"disambiguationData":[TD([[makeQuery(id+"F0.imprint","IMPRINT",EDGE,{"disambiguationData":[TD([[subQ2,-1.0]])],"derivedFrom":subQ1}),1.0]])]});}
            var Q93;
            {var subQ0=sQuery(id+"F0.wireOp",EDGE,"E3.1.1.13");var subQ1=sQuery(id+"F0.wireOp",EDGE,"E3.1.1.3");var subQ2=makeQuery(id+"F0.imprint","INTERSECT",VERTEX,{"derivedFrom":[subQ1,subQ0]});Q93=makeQuery(id+"F0.imprint","IMPRINT",FACE,{"disambiguationData":[TD([[makeQuery(id+"F0.imprint","IMPRINT",EDGE,{"disambiguationData":[TD([[subQ2,-1.0]])],"derivedFrom":subQ1}),1.0]])]});}
            var Q94;
            {var subQ0=sQuery(id+"F0.wireOp",EDGE,"E3.1.1.7");var subQ1=sQuery(id+"F0.wireOp",EDGE,"E3.1.1.1");var subQ2=makeQuery(id+"F0.imprint","INTERSECT",VERTEX,{"derivedFrom":[subQ1,subQ0]});Q94=makeQuery(id+"F0.imprint","IMPRINT",FACE,{"disambiguationData":[TD([[makeQuery(id+"F0.imprint","IMPRINT",EDGE,{"disambiguationData":[TD([[subQ2,-1.0]])],"derivedFrom":subQ1}),1.0]])]});}
            var Q95;
            {var subQ0=sQuery(id+"F0.wireOp",EDGE,"E3.1.1.10");var subQ1=sQuery(id+"F0.wireOp",EDGE,"E3.1.1.8");var subQ2=makeQuery(id+"F0.imprint","INTERSECT",VERTEX,{"derivedFrom":[subQ1,subQ0]});Q95=makeQuery(id+"F0.imprint","IMPRINT",FACE,{"disambiguationData":[TD([[makeQuery(id+"F0.imprint","IMPRINT",EDGE,{"disambiguationData":[TD([[subQ2,1.0]])],"derivedFrom":subQ1}),1.0]])]});}
            var Q96;
            {var subQ0=sQuery(id+"F0.wireOp",EDGE,"E3.1.1.18");var subQ1=sQuery(id+"F0.wireOp",EDGE,"E3.1.1.10");var subQ2=makeQuery(id+"F0.imprint","INTERSECT",VERTEX,{"derivedFrom":[subQ1,subQ0]});Q96=makeQuery(id+"F0.imprint","IMPRINT",FACE,{"disambiguationData":[TD([[makeQuery(id+"F0.imprint","IMPRINT",EDGE,{"disambiguationData":[TD([[subQ2,1.0]])],"derivedFrom":subQ1}),-1.0]])]});}
            var Q97;
            {var subQ0=sQuery(id+"F0.wireOp",EDGE,"E3.1.1.10");var subQ1=sQuery(id+"F0.wireOp",EDGE,"E3.1.1.4");var subQ2=makeQuery(id+"F0.imprint","INTERSECT",VERTEX,{"derivedFrom":[subQ1,subQ0]});Q97=makeQuery(id+"F0.imprint","IMPRINT",FACE,{"disambiguationData":[TD([[makeQuery(id+"F0.imprint","IMPRINT",EDGE,{"disambiguationData":[TD([[subQ2,1.0]])],"derivedFrom":subQ1}),-1.0]])]});}
            var Q98;
            {var subQ0=sQuery(id+"F0.wireOp",EDGE,"E3.1.1.10");var subQ1=sQuery(id+"F0.wireOp",EDGE,"E3.1.1.3");var subQ2=makeQuery(id+"F0.imprint","INTERSECT",VERTEX,{"derivedFrom":[subQ1,subQ0]});Q98=makeQuery(id+"F0.imprint","IMPRINT",FACE,{"disambiguationData":[TD([[makeQuery(id+"F0.imprint","IMPRINT",EDGE,{"disambiguationData":[TD([[subQ2,1.0]])],"derivedFrom":subQ1}),-1.0]])]});}
            var Q99;
            {var subQ0=sQuery(id+"F0.wireOp",EDGE,"E3.1.1.10");var subQ1=sQuery(id+"F0.wireOp",EDGE,"E3.1.1.6");var subQ2=makeQuery(id+"F0.imprint","INTERSECT",VERTEX,{"derivedFrom":[subQ1,subQ0]});Q99=makeQuery(id+"F0.imprint","IMPRINT",FACE,{"disambiguationData":[TD([[makeQuery(id+"F0.imprint","IMPRINT",EDGE,{"disambiguationData":[TD([[subQ2,1.0]])],"derivedFrom":subQ1}),-1.0]])]});}
            var Q100;
            {var subQ0=sQuery(id+"F0.wireOp",EDGE,"E3.1.1.15");var subQ1=sQuery(id+"F0.wireOp",EDGE,"E3.1.1.10");var subQ2=makeQuery(id+"F0.imprint","INTERSECT",VERTEX,{"derivedFrom":[subQ1,subQ0]});Q100=makeQuery(id+"F0.imprint","IMPRINT",FACE,{"disambiguationData":[TD([[makeQuery(id+"F0.imprint","IMPRINT",EDGE,{"disambiguationData":[TD([[subQ2,-1.0]])],"derivedFrom":subQ1}),-1.0]])]});}
            var Q101;
            {var subQ0=sQuery(id+"F0.wireOp",EDGE,"E3.1.1.16");var subQ1=sQuery(id+"F0.wireOp",EDGE,"E3.1.1.10");var subQ2=makeQuery(id+"F0.imprint","INTERSECT",VERTEX,{"derivedFrom":[subQ1,subQ0]});Q101=makeQuery(id+"F0.imprint","IMPRINT",FACE,{"disambiguationData":[TD([[makeQuery(id+"F0.imprint","IMPRINT",EDGE,{"disambiguationData":[TD([[subQ2,-1.0]])],"derivedFrom":subQ1}),-1.0]])]});}
            var Q102;
            {var subQ0=sQuery(id+"F0.wireOp",EDGE,"E3.1.1.19");var subQ1=sQuery(id+"F0.wireOp",EDGE,"E3.1.1.10");var subQ2=makeQuery(id+"F0.imprint","INTERSECT",VERTEX,{"derivedFrom":[subQ1,subQ0]});Q102=makeQuery(id+"F0.imprint","IMPRINT",FACE,{"disambiguationData":[TD([[makeQuery(id+"F0.imprint","IMPRINT",EDGE,{"disambiguationData":[TD([[subQ2,-1.0]])],"derivedFrom":subQ1}),-1.0]])]});}
            var Q103;
            {var subQ0=sQuery(id+"F0.wireOp",EDGE,"E3.1.1.8");var subQ1=sQuery(id+"F0.wireOp",EDGE,"E3.1.1.1");var subQ2=makeQuery(id+"F0.imprint","INTERSECT",VERTEX,{"derivedFrom":[subQ1,subQ0]});Q103=makeQuery(id+"F0.imprint","IMPRINT",FACE,{"disambiguationData":[TD([[makeQuery(id+"F0.imprint","IMPRINT",EDGE,{"disambiguationData":[TD([[subQ2,1.0]])],"derivedFrom":subQ1}),-1.0]])]});}
            var Q104;
            {var subQ0=sQuery(id+"F0.wireOp",EDGE,"E3.1.1.8");var subQ1=sQuery(id+"F0.wireOp",EDGE,"E3.1.1.1");var subQ2=makeQuery(id+"F0.imprint","INTERSECT",VERTEX,{"derivedFrom":[subQ1,subQ0]});Q104=makeQuery(id+"F0.imprint","IMPRINT",FACE,{"disambiguationData":[TD([[makeQuery(id+"F0.imprint","IMPRINT",EDGE,{"disambiguationData":[TD([[subQ2,1.0]])],"derivedFrom":subQ1}),1.0]])]});}
            var Q105;
            {var subQ0=sQuery(id+"F0.wireOp",EDGE,"E3.1.1.8");var subQ1=sQuery(id+"F0.wireOp",EDGE,"E3.1.1.2");var subQ2=makeQuery(id+"F0.imprint","INTERSECT",VERTEX,{"derivedFrom":[subQ1,subQ0]});Q105=makeQuery(id+"F0.imprint","IMPRINT",FACE,{"disambiguationData":[TD([[makeQuery(id+"F0.imprint","IMPRINT",EDGE,{"disambiguationData":[TD([[subQ2,1.0]])],"derivedFrom":subQ1}),-1.0]])]});}
            var Q106;
            {var subQ0=sQuery(id+"F0.wireOp",EDGE,"E3.1.1.8");var subQ1=sQuery(id+"F0.wireOp",EDGE,"E3.1.1.0");var subQ2=makeQuery(id+"F0.imprint","INTERSECT",VERTEX,{"derivedFrom":[subQ1,subQ0]});Q106=makeQuery(id+"F0.imprint","IMPRINT",FACE,{"disambiguationData":[TD([[makeQuery(id+"F0.imprint","IMPRINT",EDGE,{"disambiguationData":[TD([[subQ2,1.0]])],"derivedFrom":subQ1}),1.0]])]});}
            var Q107;
            {var subQ0=sQuery(id+"F0.wireOp",EDGE,"E3.1.1.8");var subQ1=sQuery(id+"F0.wireOp",EDGE,"E3.1.1.0");var subQ2=makeQuery(id+"F0.imprint","INTERSECT",VERTEX,{"derivedFrom":[subQ1,subQ0]});Q107=makeQuery(id+"F0.imprint","IMPRINT",FACE,{"disambiguationData":[TD([[makeQuery(id+"F0.imprint","IMPRINT",EDGE,{"disambiguationData":[TD([[subQ2,1.0]])],"derivedFrom":subQ1}),-1.0]])]});}
            var Q108;
            {var subQ0=sQuery(id+"F0.wireOp",EDGE,"E3.1.1.11");var subQ1=sQuery(id+"F0.wireOp",EDGE,"E3.1.1.8");var subQ2=makeQuery(id+"F0.imprint","INTERSECT",VERTEX,{"derivedFrom":[subQ1,subQ0]});Q108=makeQuery(id+"F0.imprint","IMPRINT",FACE,{"disambiguationData":[TD([[makeQuery(id+"F0.imprint","IMPRINT",EDGE,{"disambiguationData":[TD([[subQ2,-1.0]])],"derivedFrom":subQ1}),1.0]])]});}
            var Q109;
            {var subQ0=sQuery(id+"F0.wireOp",EDGE,"E3.1.1.12");var subQ1=sQuery(id+"F0.wireOp",EDGE,"E3.1.1.8");var subQ2=makeQuery(id+"F0.imprint","INTERSECT",VERTEX,{"derivedFrom":[subQ1,subQ0]});Q109=makeQuery(id+"F0.imprint","IMPRINT",FACE,{"disambiguationData":[TD([[makeQuery(id+"F0.imprint","IMPRINT",EDGE,{"disambiguationData":[TD([[subQ2,-1.0]])],"derivedFrom":subQ1}),1.0]])]});}
            var Q110;
            {var subQ0=sQuery(id+"F0.wireOp",EDGE,"E3.1.1.13");var subQ1=sQuery(id+"F0.wireOp",EDGE,"E3.1.1.8");var subQ2=makeQuery(id+"F0.imprint","INTERSECT",VERTEX,{"derivedFrom":[subQ1,subQ0]});Q110=makeQuery(id+"F0.imprint","IMPRINT",FACE,{"disambiguationData":[TD([[makeQuery(id+"F0.imprint","IMPRINT",EDGE,{"disambiguationData":[TD([[subQ2,-1.0]])],"derivedFrom":subQ1}),1.0]])]});}
            var Q111;
            {var subQ0=sQuery(id+"F0.wireOp",EDGE,"E3.1.1.12");var subQ1=sQuery(id+"F0.wireOp",EDGE,"E3.1.1.4");var subQ2=makeQuery(id+"F0.imprint","INTERSECT",VERTEX,{"derivedFrom":[subQ1,subQ0]});Q111=makeQuery(id+"F0.imprint","IMPRINT",FACE,{"disambiguationData":[TD([[makeQuery(id+"F0.imprint","IMPRINT",EDGE,{"disambiguationData":[TD([[subQ2,-1.0]])],"derivedFrom":subQ1}),-1.0]])]});}
            var Q112;
            {var subQ0=sQuery(id+"F0.wireOp",EDGE,"E3.1.1.12");var subQ1=sQuery(id+"F0.wireOp",EDGE,"E3.1.1.6");var subQ2=makeQuery(id+"F0.imprint","INTERSECT",VERTEX,{"derivedFrom":[subQ1,subQ0]});Q112=makeQuery(id+"F0.imprint","IMPRINT",FACE,{"disambiguationData":[TD([[makeQuery(id+"F0.imprint","IMPRINT",EDGE,{"disambiguationData":[TD([[subQ2,-1.0]])],"derivedFrom":subQ1}),-1.0]])]});}
            var Q113;
            {var subQ0=sQuery(id+"F0.wireOp",EDGE,"E3.1.1.15");var subQ1=sQuery(id+"F0.wireOp",EDGE,"E3.1.1.12");var subQ2=makeQuery(id+"F0.imprint","INTERSECT",VERTEX,{"derivedFrom":[subQ1,subQ0]});Q113=makeQuery(id+"F0.imprint","IMPRINT",FACE,{"disambiguationData":[TD([[makeQuery(id+"F0.imprint","IMPRINT",EDGE,{"disambiguationData":[TD([[subQ2,-1.0]])],"derivedFrom":subQ1}),1.0]])]});}
            var Q114;
            {var subQ0=sQuery(id+"F0.wireOp",EDGE,"E3.1.1.16");var subQ1=sQuery(id+"F0.wireOp",EDGE,"E3.1.1.12");var subQ2=makeQuery(id+"F0.imprint","INTERSECT",VERTEX,{"derivedFrom":[subQ1,subQ0]});Q114=makeQuery(id+"F0.imprint","IMPRINT",FACE,{"disambiguationData":[TD([[makeQuery(id+"F0.imprint","IMPRINT",EDGE,{"disambiguationData":[TD([[subQ2,-1.0]])],"derivedFrom":subQ1}),1.0]])]});}
            var Q115;
            {var subQ0=sQuery(id+"F0.wireOp",EDGE,"E3.1.1.19");var subQ1=sQuery(id+"F0.wireOp",EDGE,"E3.1.1.12");var subQ2=makeQuery(id+"F0.imprint","INTERSECT",VERTEX,{"derivedFrom":[subQ1,subQ0]});Q115=makeQuery(id+"F0.imprint","IMPRINT",FACE,{"disambiguationData":[TD([[makeQuery(id+"F0.imprint","IMPRINT",EDGE,{"disambiguationData":[TD([[subQ2,-1.0]])],"derivedFrom":subQ1}),1.0]])]});}
            var Q116;
            {var subQ0=sQuery(id+"F0.wireOp",EDGE,"E3.1.1.11");var subQ1=sQuery(id+"F0.wireOp",EDGE,"E3.1.1.4");var subQ2=makeQuery(id+"F0.imprint","INTERSECT",VERTEX,{"derivedFrom":[subQ1,subQ0]});Q116=makeQuery(id+"F0.imprint","IMPRINT",FACE,{"disambiguationData":[TD([[makeQuery(id+"F0.imprint","IMPRINT",EDGE,{"disambiguationData":[TD([[subQ2,-1.0]])],"derivedFrom":subQ1}),-1.0]])]});}
            var Q117;
            {var subQ0=sQuery(id+"F0.wireOp",EDGE,"E3.1.1.4");var subQ1=sQuery(id+"F0.wireOp",EDGE,"E3.1.1.1");var subQ2=makeQuery(id+"F0.imprint","INTERSECT",VERTEX,{"derivedFrom":[subQ1,subQ0]});Q117=makeQuery(id+"F0.imprint","IMPRINT",FACE,{"disambiguationData":[TD([[makeQuery(id+"F0.imprint","IMPRINT",EDGE,{"disambiguationData":[TD([[subQ2,-1.0]])],"derivedFrom":subQ1}),1.0]])]});}
            var Q118;
            {var subQ0=sQuery(id+"F0.wireOp",EDGE,"E3.1.1.4");var subQ1=sQuery(id+"F0.wireOp",EDGE,"E3.1.1.0");var subQ2=makeQuery(id+"F0.imprint","INTERSECT",VERTEX,{"derivedFrom":[subQ1,subQ0]});Q118=makeQuery(id+"F0.imprint","IMPRINT",FACE,{"disambiguationData":[TD([[makeQuery(id+"F0.imprint","IMPRINT",EDGE,{"disambiguationData":[TD([[subQ2,-1.0]])],"derivedFrom":subQ1}),1.0]])]});}
            var Q119;
            {var subQ0=sQuery(id+"F0.wireOp",EDGE,"E3.1.1.4");var subQ1=sQuery(id+"F0.wireOp",EDGE,"E3.1.1.0");var subQ2=makeQuery(id+"F0.imprint","INTERSECT",VERTEX,{"derivedFrom":[subQ1,subQ0]});Q119=makeQuery(id+"F0.imprint","IMPRINT",FACE,{"disambiguationData":[TD([[makeQuery(id+"F0.imprint","IMPRINT",EDGE,{"disambiguationData":[TD([[subQ2,-1.0]])],"derivedFrom":subQ1}),-1.0]])]});}
            var Q120;
            {var subQ0=sQuery(id+"F0.wireOp",EDGE,"E3.1.1.4");var subQ1=sQuery(id+"F0.wireOp",EDGE,"E3.1.1.2");var subQ2=makeQuery(id+"F0.imprint","INTERSECT",VERTEX,{"derivedFrom":[subQ1,subQ0]});Q120=makeQuery(id+"F0.imprint","IMPRINT",FACE,{"disambiguationData":[TD([[makeQuery(id+"F0.imprint","IMPRINT",EDGE,{"disambiguationData":[TD([[subQ2,-1.0]])],"derivedFrom":subQ1}),-1.0]])]});}
            var Q121;
            {var subQ0=sQuery(id+"F0.wireOp",EDGE,"E3.1.1.4");var subQ1=sQuery(id+"F0.wireOp",EDGE,"E3.1.1.1");var subQ2=makeQuery(id+"F0.imprint","INTERSECT",VERTEX,{"derivedFrom":[subQ1,subQ0]});Q121=makeQuery(id+"F0.imprint","IMPRINT",FACE,{"disambiguationData":[TD([[makeQuery(id+"F0.imprint","IMPRINT",EDGE,{"disambiguationData":[TD([[subQ2,-1.0]])],"derivedFrom":subQ1}),-1.0]])]});}
            var Q122;
            {var subQ0=sQuery(id+"F0.wireOp",EDGE,"E3.1.1.19");var subQ1=sQuery(id+"F0.wireOp",EDGE,"E3.1.1.1");var subQ2=makeQuery(id+"F0.imprint","INTERSECT",VERTEX,{"derivedFrom":[subQ1,subQ0]});Q122=makeQuery(id+"F0.imprint","IMPRINT",FACE,{"disambiguationData":[TD([[makeQuery(id+"F0.imprint","IMPRINT",EDGE,{"disambiguationData":[TD([[subQ2,-1.0]])],"derivedFrom":subQ1}),1.0]])]});}
            var Q123;
            {var subQ0=sQuery(id+"F0.wireOp",EDGE,"E3.1.1.19");var subQ1=sQuery(id+"F0.wireOp",EDGE,"E3.1.1.11");var subQ2=makeQuery(id+"F0.imprint","INTERSECT",VERTEX,{"derivedFrom":[subQ1,subQ0]});Q123=makeQuery(id+"F0.imprint","IMPRINT",FACE,{"disambiguationData":[TD([[makeQuery(id+"F0.imprint","IMPRINT",EDGE,{"disambiguationData":[TD([[subQ2,-1.0]])],"derivedFrom":subQ1}),1.0]])]});}
            var Q124;
            {var subQ0=sQuery(id+"F0.wireOp",EDGE,"E3.1.1.19");var subQ1=sQuery(id+"F0.wireOp",EDGE,"E3.1.1.2");var subQ2=makeQuery(id+"F0.imprint","INTERSECT",VERTEX,{"derivedFrom":[subQ1,subQ0]});Q124=makeQuery(id+"F0.imprint","IMPRINT",FACE,{"disambiguationData":[TD([[makeQuery(id+"F0.imprint","IMPRINT",EDGE,{"disambiguationData":[TD([[subQ2,-1.0]])],"derivedFrom":subQ1}),-1.0]])]});}
            var Q125;
            {var subQ0=sQuery(id+"F0.wireOp",EDGE,"E3.1.1.19");var subQ1=sQuery(id+"F0.wireOp",EDGE,"E3.1.1.0");var subQ2=makeQuery(id+"F0.imprint","INTERSECT",VERTEX,{"derivedFrom":[subQ1,subQ0]});Q125=makeQuery(id+"F0.imprint","IMPRINT",FACE,{"disambiguationData":[TD([[makeQuery(id+"F0.imprint","IMPRINT",EDGE,{"disambiguationData":[TD([[subQ2,-1.0]])],"derivedFrom":subQ1}),-1.0]])]});}
            var Q126;
            {var subQ0=sQuery(id+"F0.wireOp",EDGE,"E3.1.1.19");var subQ1=sQuery(id+"F0.wireOp",EDGE,"E3.1.1.0");var subQ2=makeQuery(id+"F0.imprint","INTERSECT",VERTEX,{"derivedFrom":[subQ1,subQ0]});Q126=makeQuery(id+"F0.imprint","IMPRINT",FACE,{"disambiguationData":[TD([[makeQuery(id+"F0.imprint","IMPRINT",EDGE,{"disambiguationData":[TD([[subQ2,-1.0]])],"derivedFrom":subQ1}),1.0]])]});}
            var Q127;
            {var subQ0=sQuery(id+"F0.wireOp",EDGE,"E3.1.1.19");var subQ1=sQuery(id+"F0.wireOp",EDGE,"E3.1.1.1");var subQ2=makeQuery(id+"F0.imprint","INTERSECT",VERTEX,{"derivedFrom":[subQ1,subQ0]});Q127=makeQuery(id+"F0.imprint","IMPRINT",FACE,{"disambiguationData":[TD([[makeQuery(id+"F0.imprint","IMPRINT",EDGE,{"disambiguationData":[TD([[subQ2,-1.0]])],"derivedFrom":subQ1}),-1.0]])]});}
            var Q128;
            {var subQ0=sQuery(id+"F0.wireOp",EDGE,"E3.1.1.15");var subQ1=sQuery(id+"F0.wireOp",EDGE,"E3.1.1.1");var subQ2=makeQuery(id+"F0.imprint","INTERSECT",VERTEX,{"derivedFrom":[subQ1,subQ0]});Q128=makeQuery(id+"F0.imprint","IMPRINT",FACE,{"disambiguationData":[TD([[makeQuery(id+"F0.imprint","IMPRINT",EDGE,{"disambiguationData":[TD([[subQ2,-1.0]])],"derivedFrom":subQ1}),1.0]])]});}
            var Q129;
            {var subQ0=sQuery(id+"F0.wireOp",EDGE,"E3.1.1.15");var subQ1=sQuery(id+"F0.wireOp",EDGE,"E3.1.1.0");var subQ2=makeQuery(id+"F0.imprint","INTERSECT",VERTEX,{"derivedFrom":[subQ1,subQ0]});Q129=makeQuery(id+"F0.imprint","IMPRINT",FACE,{"disambiguationData":[TD([[makeQuery(id+"F0.imprint","IMPRINT",EDGE,{"disambiguationData":[TD([[subQ2,-1.0]])],"derivedFrom":subQ1}),1.0]])]});}
            var Q130;
            {var subQ0=sQuery(id+"F0.wireOp",EDGE,"E3.1.1.15");var subQ1=sQuery(id+"F0.wireOp",EDGE,"E3.1.1.0");var subQ2=makeQuery(id+"F0.imprint","INTERSECT",VERTEX,{"derivedFrom":[subQ1,subQ0]});Q130=makeQuery(id+"F0.imprint","IMPRINT",FACE,{"disambiguationData":[TD([[makeQuery(id+"F0.imprint","IMPRINT",EDGE,{"disambiguationData":[TD([[subQ2,-1.0]])],"derivedFrom":subQ1}),-1.0]])]});}
            var Q131;
            {var subQ0=sQuery(id+"F0.wireOp",EDGE,"E3.1.1.15");var subQ1=sQuery(id+"F0.wireOp",EDGE,"E3.1.1.2");var subQ2=makeQuery(id+"F0.imprint","INTERSECT",VERTEX,{"derivedFrom":[subQ1,subQ0]});Q131=makeQuery(id+"F0.imprint","IMPRINT",FACE,{"disambiguationData":[TD([[makeQuery(id+"F0.imprint","IMPRINT",EDGE,{"disambiguationData":[TD([[subQ2,-1.0]])],"derivedFrom":subQ1}),-1.0]])]});}
            var Q132;
            {var subQ0=sQuery(id+"F0.wireOp",EDGE,"E3.1.1.15");var subQ1=sQuery(id+"F0.wireOp",EDGE,"E3.1.1.1");var subQ2=makeQuery(id+"F0.imprint","INTERSECT",VERTEX,{"derivedFrom":[subQ1,subQ0]});Q132=makeQuery(id+"F0.imprint","IMPRINT",FACE,{"disambiguationData":[TD([[makeQuery(id+"F0.imprint","IMPRINT",EDGE,{"disambiguationData":[TD([[subQ2,-1.0]])],"derivedFrom":subQ1}),-1.0]])]});}
            extrude(context, id + "F2", {"entities" : qUnion([Q0, Q1, Q2, Q3, Q4, Q5, Q6, Q7, Q8, Q9, Q10, Q11, Q12, Q13, Q14, Q15, Q16, Q17, Q18, Q19, Q20, Q21, Q22, Q23, Q24, Q25, Q26, Q27, Q28, Q29, Q30, Q31, Q32, Q33, Q34, Q35, Q36, Q37, Q38, Q39, Q40, Q41, Q42, Q43, Q44, Q45, Q46, Q47, Q48, Q49, Q50, Q51, Q52, Q53, Q54, Q55, Q56, Q57, Q58, Q59, Q60, Q61, Q62, Q63, Q64, Q65, Q66, Q67, Q68, Q69, Q70, Q71, Q72, Q73, Q74, Q75, Q76, Q77, Q78, Q79, Q80, Q81, Q82, Q83, Q84, Q85, Q86, Q87, Q88, Q89, Q90, Q91, Q92, Q93, Q94, Q95, Q96, Q97, Q98, Q99, Q100, Q101, Q102, Q103, Q104, Q105, Q106, Q107, Q108, Q109, Q110, Q111, Q112, Q113, Q114, Q115, Q116, Q117, Q118, Q119, Q120, Q121, Q122, Q123, Q124, Q125, Q126, Q127, Q128, Q129, Q130, Q131, Q132]), "operationType" : NewBodyOperationType.ADD, "depth" : 25.4 * mm});
        }
        {
            var Q0;
            {var subQ0=sQuery(id+"F0.wireOp",EDGE,"E2.0.2.0");var subQ1=sQuery(id+"F0.wireOp",EDGE,"E0.right");var subQ2=makeQuery(id+"F0.imprint","INTERSECT",VERTEX,{"derivedFrom":[subQ1,subQ0]});Q0=makeQuery(id+"F0.imprint","IMPRINT",FACE,{"disambiguationData":[TD([[makeQuery(id+"F0.imprint","IMPRINT",EDGE,{"disambiguationData":[TD([[subQ2,-1.0]])],"derivedFrom":subQ1}),-1.0]])]});}
            var Q1;
            {var subQ0=sQuery(id+"F0.wireOp",EDGE,"E2.0.2.0");var subQ1=sQuery(id+"F0.wireOp",EDGE,"E1.7.0.0");var subQ2=makeQuery(id+"F0.imprint","INTERSECT",VERTEX,{"derivedFrom":[subQ1,subQ0]});Q1=makeQuery(id+"F0.imprint","IMPRINT",FACE,{"disambiguationData":[TD([[makeQuery(id+"F0.imprint","IMPRINT",EDGE,{"disambiguationData":[TD([[subQ2,-1.0]])],"derivedFrom":subQ1}),1.0]])]});}
            var Q2;
            {var subQ0=sQuery(id+"F0.wireOp",EDGE,"E2.0.2.0");var subQ1=sQuery(id+"F0.wireOp",EDGE,"E1.6.0.0");var subQ2=makeQuery(id+"F0.imprint","INTERSECT",VERTEX,{"derivedFrom":[subQ1,subQ0]});Q2=makeQuery(id+"F0.imprint","IMPRINT",FACE,{"disambiguationData":[TD([[makeQuery(id+"F0.imprint","IMPRINT",EDGE,{"disambiguationData":[TD([[subQ2,-1.0]])],"derivedFrom":subQ1}),1.0]])]});}
            var Q3;
            {var subQ0=sQuery(id+"F0.wireOp",EDGE,"E2.0.2.0");var subQ1=sQuery(id+"F0.wireOp",EDGE,"E1.5.0.0");var subQ2=makeQuery(id+"F0.imprint","INTERSECT",VERTEX,{"derivedFrom":[subQ1,subQ0]});Q3=makeQuery(id+"F0.imprint","IMPRINT",FACE,{"disambiguationData":[TD([[makeQuery(id+"F0.imprint","IMPRINT",EDGE,{"disambiguationData":[TD([[subQ2,-1.0]])],"derivedFrom":subQ1}),1.0]])]});}
            var Q4;
            {var subQ0=sQuery(id+"F0.wireOp",EDGE,"E2.0.2.0");var subQ1=sQuery(id+"F0.wireOp",EDGE,"E1.4.0.0");var subQ2=makeQuery(id+"F0.imprint","INTERSECT",VERTEX,{"derivedFrom":[subQ1,subQ0]});Q4=makeQuery(id+"F0.imprint","IMPRINT",FACE,{"disambiguationData":[TD([[makeQuery(id+"F0.imprint","IMPRINT",EDGE,{"disambiguationData":[TD([[subQ2,-1.0]])],"derivedFrom":subQ1}),1.0]])]});}
            var Q5;
            {var subQ0=sQuery(id+"F0.wireOp",EDGE,"E2.0.2.0");var subQ1=sQuery(id+"F0.wireOp",EDGE,"E1.3.0.0");var subQ2=makeQuery(id+"F0.imprint","INTERSECT",VERTEX,{"derivedFrom":[subQ1,subQ0]});Q5=makeQuery(id+"F0.imprint","IMPRINT",FACE,{"disambiguationData":[TD([[makeQuery(id+"F0.imprint","IMPRINT",EDGE,{"disambiguationData":[TD([[subQ2,-1.0]])],"derivedFrom":subQ1}),1.0]])]});}
            var Q6;
            {var subQ0=sQuery(id+"F0.wireOp",EDGE,"E2.0.2.0");var subQ1=sQuery(id+"F0.wireOp",EDGE,"E1.2.0.0");var subQ2=makeQuery(id+"F0.imprint","INTERSECT",VERTEX,{"derivedFrom":[subQ1,subQ0]});Q6=makeQuery(id+"F0.imprint","IMPRINT",FACE,{"disambiguationData":[TD([[makeQuery(id+"F0.imprint","IMPRINT",EDGE,{"disambiguationData":[TD([[subQ2,-1.0]])],"derivedFrom":subQ1}),1.0]])]});}
            extrude(context, id + "F3", {"entities" : qUnion([Q0, Q1, Q2, Q3, Q4, Q5, Q6]), "depth" : 25.4 * mm});
        }
        {
            var Q0;
            Q0=qCreatedBy(makeId("Front.planeOp"),FACE);
            var sketch = newSketch(context, id + "F4", { "sketchPlane" : qUnion([Q0])});
            skPoint(sketch, "E26.0", {"position": v(114.3, -114.3) * mm});
            skPoint(sketch, "E27.0", {"position": v(139.7, -139.7) * mm});
            skLineSegment(sketch, "E28", {"start": v(114.3, -114.3) * mm, "end": v(139.7, -139.7) * mm});
            skLineSegment(sketch, "E29.bottom", {"start": v(-144.07, -398.07) * mm, "end": v(398.07, -398.07) * mm});
            skLineSegment(sketch, "E29.top", {"start": v(-144.07, 144.07) * mm, "end": v(398.07, 144.07) * mm});
            skLineSegment(sketch, "E29.left", {"start": v(-144.07, -398.07) * mm, "end": v(-144.07, 144.07) * mm});
            skLineSegment(sketch, "E29.right", {"start": v(398.07, -398.07) * mm, "end": v(398.07, 144.07) * mm});
            skPoint(sketch, "E29.middle", {"position": v(127, -127) * mm});
            skCircle(sketch, "E30", {"center": v(127, 224.64) * mm, "radius": 38.1 * mm});
            skCircle(sketch, "E31.0", {"center": v(127, 224.64) * mm, "radius": 63.5 * mm});
            skFitSpline(sketch, "E32", {"points": [v(-144.07, 144.07) * mm, v(0, 200.27) * mm, v(81, 268.42) * mm], "startDerivative": vector(221.9, 0) * mm, "endDerivative": vector(188.33, 197.9) * mm});
            skLineSegment(sketch, "E33", {"start": v(127, -127) * mm, "end": v(127, 144.07) * mm, "construction": true});
            skFitSpline(sketch, "E34.MirrorCS", {"points": [v(398.07, 144.07) * mm, v(254, 200.27) * mm, v(173, 268.42) * mm], "startDerivative": vector(-221.9, 0) * mm, "endDerivative": vector(-188.33, 197.9) * mm});
            skSolve(sketch);
        }
        {
            var Q0;
            Q0 = qSketchRegion(id + "F4", true);
            extrude(context, id + "F5", {"entities" : qUnion([Q0]), "oppositeDirection" : true, "depth" : 25.4 * mm});
        }
    });
